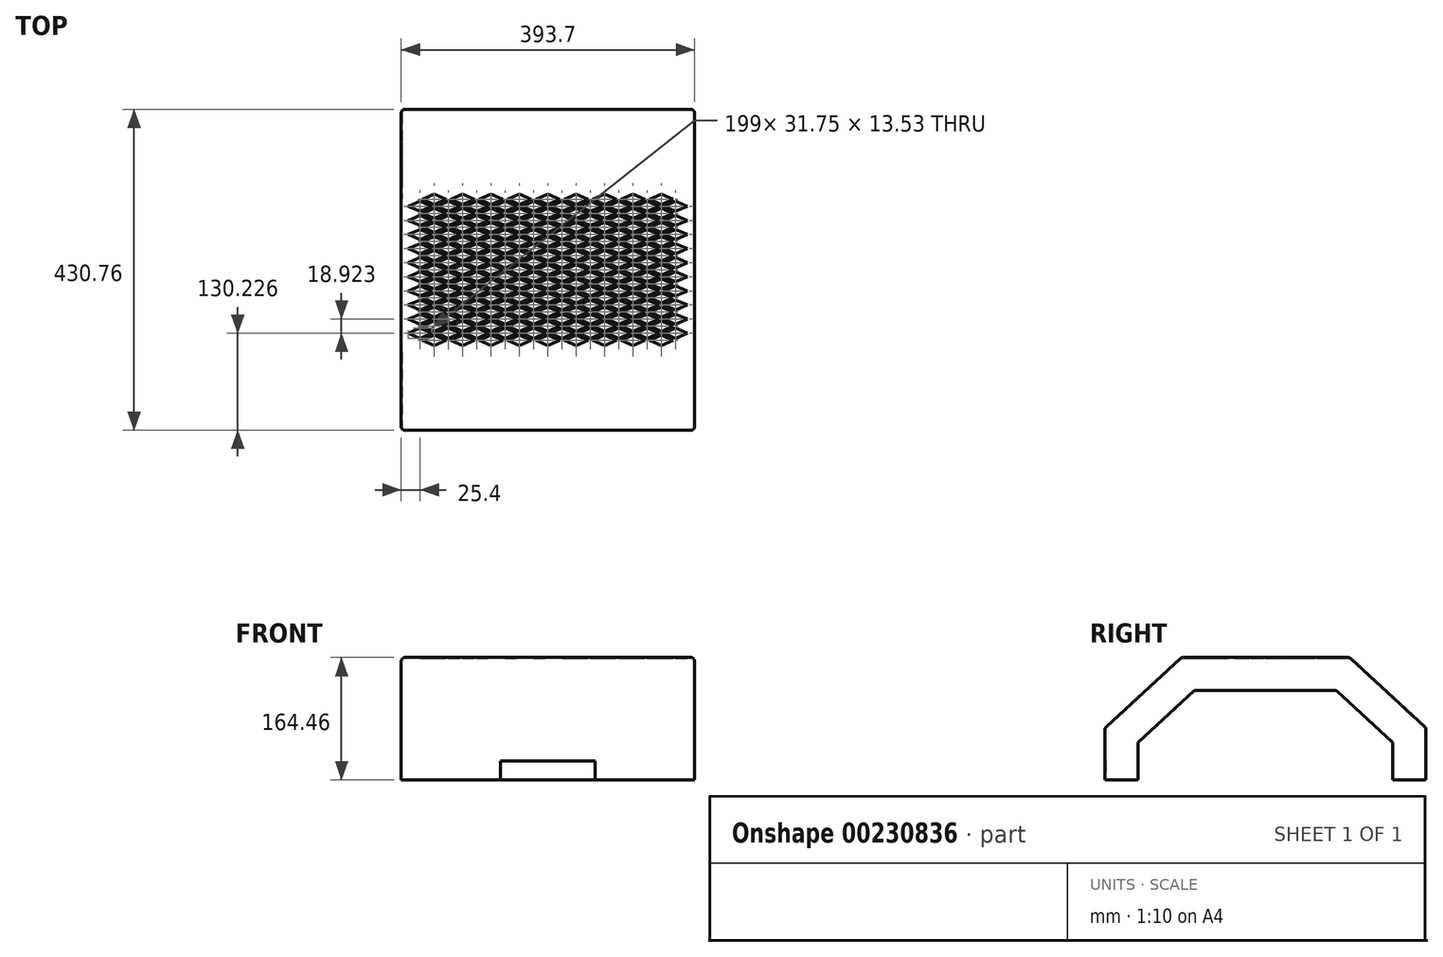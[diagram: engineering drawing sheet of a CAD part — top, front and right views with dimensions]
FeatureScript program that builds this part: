
annotation { "Feature Type Name" : "Feature", "Feature Type Description" : "" }
export const myFeature = defineFeature(function(context is Context, id is Id, definition is map)
    precondition{}
    {
        {
            var Q0;
            Q0=qCreatedBy(makeId("Right.planeOp"),FACE);
            var sketch = newSketch(context, id + "F0", { "sketchPlane" : qUnion([Q0])});
            skLineSegment(sketch, "E0", {"start": v(0, 0) * mm, "end": v(0, 169.27) * mm, "construction": true});
            skLineSegment(sketch, "E1", {"start": v(0, 164.46) * mm, "end": v(112.6, 164.46) * mm});
            skLineSegment(sketch, "E2", {"start": v(112.6, 164.46) * mm, "end": v(215.38, 69.85) * mm});
            skLineSegment(sketch, "E3", {"start": v(215.38, 69.85) * mm, "end": v(215.38, 0) * mm});
            skLineSegment(sketch, "E4", {"start": v(215.38, 0) * mm, "end": v(170.93, 0) * mm});
            skLineSegment(sketch, "E5", {"start": v(170.93, 0) * mm, "end": v(170.93, 50.35) * mm});
            skLineSegment(sketch, "E6", {"start": v(170.93, 50.35) * mm, "end": v(95.25, 120.01) * mm});
            skLineSegment(sketch, "E7", {"start": v(95.25, 120.01) * mm, "end": v(0, 120.01) * mm});
            skLineSegment(sketch, "E8.MirrorCS", {"start": v(0, 164.46) * mm, "end": v(-112.6, 164.46) * mm});
            skLineSegment(sketch, "E9.MirrorCS", {"start": v(-215.38, 0) * mm, "end": v(-170.93, 0) * mm});
            skLineSegment(sketch, "E10.MirrorCS", {"start": v(-170.93, 0) * mm, "end": v(-170.93, 50.35) * mm});
            skLineSegment(sketch, "E11.MirrorCS", {"start": v(-215.38, 69.85) * mm, "end": v(-215.38, 0) * mm});
            skLineSegment(sketch, "E12.MirrorCS", {"start": v(-95.25, 120.01) * mm, "end": v(0, 120.01) * mm});
            skLineSegment(sketch, "E13.MirrorCS", {"start": v(-112.6, 164.46) * mm, "end": v(-215.38, 69.85) * mm});
            skLineSegment(sketch, "E14.MirrorCS", {"start": v(-170.93, 50.35) * mm, "end": v(-95.25, 120.01) * mm});
            skSolve(sketch);
        }
        {
            var Q0;
            Q0=qSketchRegion(id+"F0",true);
            extrude(context, id + "F1", {"entities" : qUnion([Q0]), "endBound" : BoundingType.SYMMETRIC, "depth" : 393.7 * mm});
        }
        {
            var Q0;
            Q0=makeQuery(id+"F1.opExtrude","CAP_EDGE",EDGE,{"disambiguationData":[OSD([sQuery(id+"F0.wireOp",EDGE,"E1"),sQuery(id+"F0.wireOp",EDGE,"E8.MirrorCS")])],"isStart":true});
            var Q1;
            Q1=makeQuery(id+"F1.opExtrude","CAP_EDGE",EDGE,{"disambiguationData":[OSD([sQuery(id+"F0.wireOp",EDGE,"E1"),sQuery(id+"F0.wireOp",EDGE,"E8.MirrorCS")])],"isStart":false});
            var Q2;
            Q2=makeQuery(id+"F1.opExtrude","CAP_EDGE",EDGE,{"disambiguationData":[OSD([sQuery(id+"F0.wireOp",EDGE,"E13.MirrorCS")])],"isStart":false});
            var Q3;
            Q3=makeQuery(id+"F1.opExtrude","CAP_EDGE",EDGE,{"disambiguationData":[OSD([sQuery(id+"F0.wireOp",EDGE,"E11.MirrorCS")])],"isStart":false});
            var Q4;
            Q4=makeQuery(id+"F1.opExtrude","CAP_EDGE",EDGE,{"disambiguationData":[OSD([sQuery(id+"F0.wireOp",EDGE,"E2")])],"isStart":false});
            var Q5;
            Q5=makeQuery(id+"F1.opExtrude","CAP_EDGE",EDGE,{"disambiguationData":[OSD([sQuery(id+"F0.wireOp",EDGE,"E3")])],"isStart":false});
            var Q6;
            Q6=makeQuery(id+"F1.opExtrude","CAP_EDGE",EDGE,{"disambiguationData":[OSD([sQuery(id+"F0.wireOp",EDGE,"E3")])],"isStart":true});
            var Q7;
            Q7=makeQuery(id+"F1.opExtrude","CAP_EDGE",EDGE,{"disambiguationData":[OSD([sQuery(id+"F0.wireOp",EDGE,"E2")])],"isStart":true});
            var Q8;
            Q8=makeQuery(id+"F1.opExtrude","CAP_EDGE",EDGE,{"disambiguationData":[OSD([sQuery(id+"F0.wireOp",EDGE,"E13.MirrorCS")])],"isStart":true});
            var Q9;
            Q9=makeQuery(id+"F1.opExtrude","CAP_EDGE",EDGE,{"disambiguationData":[OSD([sQuery(id+"F0.wireOp",EDGE,"E11.MirrorCS")])],"isStart":true});
            var Q10;
            Q10=makeQuery(id+"F1.opExtrude","SWEPT_EDGE",EDGE,{"disambiguationData":[OSD([sQuery(id+"F0.wireOp",EDGE,"E11.MirrorCS"),sQuery(id+"F0.wireOp",EDGE,"E13.MirrorCS")])]});
            var Q11;
            Q11=makeQuery(id+"F1.opExtrude","SWEPT_EDGE",EDGE,{"disambiguationData":[OSD([sQuery(id+"F0.wireOp",EDGE,"E8.MirrorCS"),sQuery(id+"F0.wireOp",EDGE,"E13.MirrorCS")])]});
            var Q12;
            Q12=makeQuery(id+"F1.opExtrude","SWEPT_EDGE",EDGE,{"disambiguationData":[OSD([sQuery(id+"F0.wireOp",EDGE,"E1"),sQuery(id+"F0.wireOp",EDGE,"E2")])]});
            var Q13;
            Q13=makeQuery(id+"F1.opExtrude","SWEPT_EDGE",EDGE,{"disambiguationData":[OSD([sQuery(id+"F0.wireOp",EDGE,"E2"),sQuery(id+"F0.wireOp",EDGE,"E3")])]});
            fillet(context, id + "F2", {"entities" : qUnion([Q0, Q1, Q2, Q3, Q4, Q5, Q6, Q7, Q8, Q9, Q10, Q11, Q12, Q13]), "radius" : 5.08 * mm, "tangentPropagation" : true, "allowEdgeOverflow" : false});
        }
        {
            var Q0;
            Q0=makeQuery(id+"F1.opExtrude","SWEPT_FACE",FACE,{"disambiguationData":[OSD([sQuery(id+"F0.wireOp",EDGE,"E7"),sQuery(id+"F0.wireOp",EDGE,"E12.MirrorCS")])]});
            var Q1;
            Q1=makeQuery(id+"F1.opExtrude","SWEPT_FACE",FACE,{"disambiguationData":[OSD([sQuery(id+"F0.wireOp",EDGE,"E6")])]});
            var Q2;
            Q2=makeQuery(id+"F1.opExtrude","SWEPT_FACE",FACE,{"disambiguationData":[OSD([sQuery(id+"F0.wireOp",EDGE,"E5")])]});
            var Q3;
            Q3=makeQuery(id+"F1.opExtrude","SWEPT_FACE",FACE,{"disambiguationData":[OSD([sQuery(id+"F0.wireOp",EDGE,"E4")])]});
            var Q4;
            Q4=makeQuery(id+"F1.opExtrude","SWEPT_FACE",FACE,{"disambiguationData":[OSD([sQuery(id+"F0.wireOp",EDGE,"E14.MirrorCS")])]});
            var Q5;
            Q5=makeQuery(id+"F1.opExtrude","SWEPT_FACE",FACE,{"disambiguationData":[OSD([sQuery(id+"F0.wireOp",EDGE,"E10.MirrorCS")])]});
            var Q6;
            Q6=makeQuery(id+"F1.opExtrude","SWEPT_FACE",FACE,{"disambiguationData":[OSD([sQuery(id+"F0.wireOp",EDGE,"E9.MirrorCS")])]});
            shell(context, id + "F3", {"entities" : qUnion([Q0, Q1, Q2, Q3, Q4, Q5, Q6]), "thickness" : 0.95 * mm});
        }
        {
            var Q0;
            Q0=makeQuery(id+"F1.opExtrude","SWEPT_FACE",FACE,{"disambiguationData":[OSD([sQuery(id+"F0.wireOp",EDGE,"E11.MirrorCS")])]});
            var sketch = newSketch(context, id + "F4", { "sketchPlane" : qUnion([Q0])});
            skLineSegment(sketch, "E15.bottom", {"start": v(-63.5, 0) * mm, "end": v(63.5, 0) * mm});
            skLineSegment(sketch, "E15.top", {"start": v(-63.5, 25.4) * mm, "end": v(63.5, 25.4) * mm});
            skLineSegment(sketch, "E15.left", {"start": v(-63.5, 0) * mm, "end": v(-63.5, 25.4) * mm});
            skLineSegment(sketch, "E15.right", {"start": v(63.5, 0) * mm, "end": v(63.5, 25.4) * mm});
            skSolve(sketch);
        }
        {
            var Q0;
            Q0=qSketchRegion(id+"F4",true);
            extrude(context, id + "F5", {"entities" : qUnion([Q0]), "operationType" : NewBodyOperationType.REMOVE, "oppositeDirection" : true, "depth" : 25.4 * mm});
        }
        {
            var Q0;
            Q0=makeQuery(id+"F1.opExtrude","SWEPT_FACE",FACE,{"disambiguationData":[OSD([sQuery(id+"F0.wireOp",EDGE,"E1"),sQuery(id+"F0.wireOp",EDGE,"E8.MirrorCS")])]});
            var sketch = newSketch(context, id + "F6", { "sketchPlane" : qUnion([Q0])});
            skLineSegment(sketch, "E16", {"start": v(-15.88, 0) * mm, "end": v(0, 6.76) * mm});
            skLineSegment(sketch, "E17", {"start": v(0, 6.76) * mm, "end": v(15.88, 0) * mm});
            skLineSegment(sketch, "E18", {"start": v(15.88, 0) * mm, "end": v(0, -6.76) * mm});
            skLineSegment(sketch, "E19", {"start": v(0, -6.76) * mm, "end": v(-15.88, 0) * mm});
            skLineSegment(sketch, "E20.0.1.0", {"start": v(-15.88, 18.92) * mm, "end": v(0, 25.69) * mm});
            skLineSegment(sketch, "E20.0.1.1", {"start": v(15.88, 18.92) * mm, "end": v(0, 12.16) * mm});
            skLineSegment(sketch, "E20.0.1.2", {"start": v(0, 12.16) * mm, "end": v(-15.88, 18.92) * mm});
            skLineSegment(sketch, "E20.0.1.3", {"start": v(0, 25.69) * mm, "end": v(15.88, 18.92) * mm});
            skLineSegment(sketch, "E20.0.2.0", {"start": v(-15.88, 37.85) * mm, "end": v(0, 44.6) * mm});
            skLineSegment(sketch, "E20.0.2.1", {"start": v(15.88, 37.85) * mm, "end": v(0, 31.08) * mm});
            skLineSegment(sketch, "E20.0.2.2", {"start": v(0, 31.08) * mm, "end": v(-15.88, 37.85) * mm});
            skLineSegment(sketch, "E20.0.2.3", {"start": v(0, 44.6) * mm, "end": v(15.88, 37.85) * mm});
            skLineSegment(sketch, "E20.0.3.0", {"start": v(-15.88, 56.77) * mm, "end": v(0, 63.53) * mm});
            skLineSegment(sketch, "E20.0.3.1", {"start": v(15.88, 56.77) * mm, "end": v(0, 50) * mm});
            skLineSegment(sketch, "E20.0.3.2", {"start": v(0, 50) * mm, "end": v(-15.88, 56.77) * mm});
            skLineSegment(sketch, "E20.0.3.3", {"start": v(0, 63.53) * mm, "end": v(15.88, 56.77) * mm});
            skLineSegment(sketch, "E20.0.4.0", {"start": v(-15.88, 75.7) * mm, "end": v(0, 82.45) * mm});
            skLineSegment(sketch, "E20.0.4.1", {"start": v(15.88, 75.7) * mm, "end": v(0, 68.93) * mm});
            skLineSegment(sketch, "E20.0.4.2", {"start": v(0, 68.93) * mm, "end": v(-15.88, 75.7) * mm});
            skLineSegment(sketch, "E20.0.4.3", {"start": v(0, 82.45) * mm, "end": v(15.88, 75.7) * mm});
            skLineSegment(sketch, "E20.0.5.0", {"start": v(-15.88, 94.62) * mm, "end": v(0, 101.38) * mm});
            skLineSegment(sketch, "E20.0.5.1", {"start": v(15.88, 94.62) * mm, "end": v(0, 87.85) * mm});
            skLineSegment(sketch, "E20.0.5.2", {"start": v(0, 87.85) * mm, "end": v(-15.88, 94.62) * mm});
            skLineSegment(sketch, "E20.0.5.3", {"start": v(0, 101.38) * mm, "end": v(15.88, 94.62) * mm});
            skLineSegment(sketch, "E20.1.0.0", {"start": v(22.23, 0) * mm, "end": v(38.1, 6.76) * mm});
            skLineSegment(sketch, "E20.1.0.1", {"start": v(53.98, 0) * mm, "end": v(38.1, -6.76) * mm});
            skLineSegment(sketch, "E20.1.0.2", {"start": v(38.1, -6.76) * mm, "end": v(22.22, 0) * mm});
            skLineSegment(sketch, "E20.1.0.3", {"start": v(38.1, 6.76) * mm, "end": v(53.98, 0) * mm});
            skLineSegment(sketch, "E20.1.1.0", {"start": v(22.23, 18.92) * mm, "end": v(38.1, 25.69) * mm});
            skLineSegment(sketch, "E20.1.1.1", {"start": v(53.98, 18.92) * mm, "end": v(38.1, 12.16) * mm});
            skLineSegment(sketch, "E20.1.1.2", {"start": v(38.1, 12.16) * mm, "end": v(22.22, 18.92) * mm});
            skLineSegment(sketch, "E20.1.1.3", {"start": v(38.1, 25.69) * mm, "end": v(53.98, 18.92) * mm});
            skLineSegment(sketch, "E20.1.2.0", {"start": v(22.23, 37.85) * mm, "end": v(38.1, 44.6) * mm});
            skLineSegment(sketch, "E20.1.2.1", {"start": v(53.98, 37.85) * mm, "end": v(38.1, 31.08) * mm});
            skLineSegment(sketch, "E20.1.2.2", {"start": v(38.1, 31.08) * mm, "end": v(22.22, 37.85) * mm});
            skLineSegment(sketch, "E20.1.2.3", {"start": v(38.1, 44.6) * mm, "end": v(53.98, 37.85) * mm});
            skLineSegment(sketch, "E20.1.3.0", {"start": v(22.23, 56.77) * mm, "end": v(38.1, 63.53) * mm});
            skLineSegment(sketch, "E20.1.3.1", {"start": v(53.98, 56.77) * mm, "end": v(38.1, 50) * mm});
            skLineSegment(sketch, "E20.1.3.2", {"start": v(38.1, 50) * mm, "end": v(22.22, 56.77) * mm});
            skLineSegment(sketch, "E20.1.3.3", {"start": v(38.1, 63.53) * mm, "end": v(53.98, 56.77) * mm});
            skLineSegment(sketch, "E20.1.4.0", {"start": v(22.23, 75.7) * mm, "end": v(38.1, 82.45) * mm});
            skLineSegment(sketch, "E20.1.4.1", {"start": v(53.98, 75.7) * mm, "end": v(38.1, 68.93) * mm});
            skLineSegment(sketch, "E20.1.4.2", {"start": v(38.1, 68.93) * mm, "end": v(22.22, 75.7) * mm});
            skLineSegment(sketch, "E20.1.4.3", {"start": v(38.1, 82.45) * mm, "end": v(53.98, 75.7) * mm});
            skLineSegment(sketch, "E20.1.5.0", {"start": v(22.23, 94.62) * mm, "end": v(38.1, 101.38) * mm});
            skLineSegment(sketch, "E20.1.5.1", {"start": v(53.98, 94.62) * mm, "end": v(38.1, 87.85) * mm});
            skLineSegment(sketch, "E20.1.5.2", {"start": v(38.1, 87.85) * mm, "end": v(22.22, 94.62) * mm});
            skLineSegment(sketch, "E20.1.5.3", {"start": v(38.1, 101.38) * mm, "end": v(53.98, 94.62) * mm});
            skLineSegment(sketch, "E20.2.0.0", {"start": v(60.33, 0) * mm, "end": v(76.2, 6.76) * mm});
            skLineSegment(sketch, "E20.2.0.1", {"start": v(92.08, 0) * mm, "end": v(76.2, -6.76) * mm});
            skLineSegment(sketch, "E20.2.0.2", {"start": v(76.2, -6.76) * mm, "end": v(60.33, 0) * mm});
            skLineSegment(sketch, "E20.2.0.3", {"start": v(76.2, 6.76) * mm, "end": v(92.08, 0) * mm});
            skLineSegment(sketch, "E20.2.1.0", {"start": v(60.33, 18.92) * mm, "end": v(76.2, 25.69) * mm});
            skLineSegment(sketch, "E20.2.1.1", {"start": v(92.08, 18.92) * mm, "end": v(76.2, 12.16) * mm});
            skLineSegment(sketch, "E20.2.1.2", {"start": v(76.2, 12.16) * mm, "end": v(60.33, 18.92) * mm});
            skLineSegment(sketch, "E20.2.1.3", {"start": v(76.2, 25.69) * mm, "end": v(92.08, 18.92) * mm});
            skLineSegment(sketch, "E20.2.2.0", {"start": v(60.33, 37.85) * mm, "end": v(76.2, 44.6) * mm});
            skLineSegment(sketch, "E20.2.2.1", {"start": v(92.08, 37.85) * mm, "end": v(76.2, 31.08) * mm});
            skLineSegment(sketch, "E20.2.2.2", {"start": v(76.2, 31.08) * mm, "end": v(60.33, 37.85) * mm});
            skLineSegment(sketch, "E20.2.2.3", {"start": v(76.2, 44.6) * mm, "end": v(92.08, 37.85) * mm});
            skLineSegment(sketch, "E20.2.3.0", {"start": v(60.33, 56.77) * mm, "end": v(76.2, 63.53) * mm});
            skLineSegment(sketch, "E20.2.3.1", {"start": v(92.08, 56.77) * mm, "end": v(76.2, 50) * mm});
            skLineSegment(sketch, "E20.2.3.2", {"start": v(76.2, 50) * mm, "end": v(60.33, 56.77) * mm});
            skLineSegment(sketch, "E20.2.3.3", {"start": v(76.2, 63.53) * mm, "end": v(92.08, 56.77) * mm});
            skLineSegment(sketch, "E20.2.4.0", {"start": v(60.33, 75.7) * mm, "end": v(76.2, 82.45) * mm});
            skLineSegment(sketch, "E20.2.4.1", {"start": v(92.08, 75.7) * mm, "end": v(76.2, 68.93) * mm});
            skLineSegment(sketch, "E20.2.4.2", {"start": v(76.2, 68.93) * mm, "end": v(60.33, 75.7) * mm});
            skLineSegment(sketch, "E20.2.4.3", {"start": v(76.2, 82.45) * mm, "end": v(92.08, 75.7) * mm});
            skLineSegment(sketch, "E20.2.5.0", {"start": v(60.33, 94.62) * mm, "end": v(76.2, 101.38) * mm});
            skLineSegment(sketch, "E20.2.5.1", {"start": v(92.08, 94.62) * mm, "end": v(76.2, 87.85) * mm});
            skLineSegment(sketch, "E20.2.5.2", {"start": v(76.2, 87.85) * mm, "end": v(60.33, 94.62) * mm});
            skLineSegment(sketch, "E20.2.5.3", {"start": v(76.2, 101.38) * mm, "end": v(92.08, 94.62) * mm});
            skLineSegment(sketch, "E20.3.0.0", {"start": v(98.43, 0) * mm, "end": v(114.3, 6.76) * mm});
            skLineSegment(sketch, "E20.3.0.1", {"start": v(130.18, 0) * mm, "end": v(114.3, -6.76) * mm});
            skLineSegment(sketch, "E20.3.0.2", {"start": v(114.3, -6.76) * mm, "end": v(98.43, 0) * mm});
            skLineSegment(sketch, "E20.3.0.3", {"start": v(114.3, 6.76) * mm, "end": v(130.18, 0) * mm});
            skLineSegment(sketch, "E20.3.1.0", {"start": v(98.43, 18.92) * mm, "end": v(114.3, 25.69) * mm});
            skLineSegment(sketch, "E20.3.1.1", {"start": v(130.18, 18.92) * mm, "end": v(114.3, 12.16) * mm});
            skLineSegment(sketch, "E20.3.1.2", {"start": v(114.3, 12.16) * mm, "end": v(98.43, 18.92) * mm});
            skLineSegment(sketch, "E20.3.1.3", {"start": v(114.3, 25.69) * mm, "end": v(130.18, 18.92) * mm});
            skLineSegment(sketch, "E20.3.2.0", {"start": v(98.43, 37.85) * mm, "end": v(114.3, 44.6) * mm});
            skLineSegment(sketch, "E20.3.2.1", {"start": v(130.18, 37.85) * mm, "end": v(114.3, 31.08) * mm});
            skLineSegment(sketch, "E20.3.2.2", {"start": v(114.3, 31.08) * mm, "end": v(98.43, 37.85) * mm});
            skLineSegment(sketch, "E20.3.2.3", {"start": v(114.3, 44.6) * mm, "end": v(130.18, 37.85) * mm});
            skLineSegment(sketch, "E20.3.3.0", {"start": v(98.43, 56.77) * mm, "end": v(114.3, 63.53) * mm});
            skLineSegment(sketch, "E20.3.3.1", {"start": v(130.18, 56.77) * mm, "end": v(114.3, 50) * mm});
            skLineSegment(sketch, "E20.3.3.2", {"start": v(114.3, 50) * mm, "end": v(98.43, 56.77) * mm});
            skLineSegment(sketch, "E20.3.3.3", {"start": v(114.3, 63.53) * mm, "end": v(130.18, 56.77) * mm});
            skLineSegment(sketch, "E20.3.4.0", {"start": v(98.43, 75.7) * mm, "end": v(114.3, 82.45) * mm});
            skLineSegment(sketch, "E20.3.4.1", {"start": v(130.18, 75.7) * mm, "end": v(114.3, 68.93) * mm});
            skLineSegment(sketch, "E20.3.4.2", {"start": v(114.3, 68.93) * mm, "end": v(98.43, 75.7) * mm});
            skLineSegment(sketch, "E20.3.4.3", {"start": v(114.3, 82.45) * mm, "end": v(130.18, 75.7) * mm});
            skLineSegment(sketch, "E20.3.5.0", {"start": v(98.43, 94.62) * mm, "end": v(114.3, 101.38) * mm});
            skLineSegment(sketch, "E20.3.5.1", {"start": v(130.18, 94.62) * mm, "end": v(114.3, 87.85) * mm});
            skLineSegment(sketch, "E20.3.5.2", {"start": v(114.3, 87.85) * mm, "end": v(98.43, 94.62) * mm});
            skLineSegment(sketch, "E20.3.5.3", {"start": v(114.3, 101.38) * mm, "end": v(130.18, 94.62) * mm});
            skLineSegment(sketch, "E20.4.0.0", {"start": v(136.53, 0) * mm, "end": v(152.4, 6.76) * mm});
            skLineSegment(sketch, "E20.4.0.1", {"start": v(168.28, 0) * mm, "end": v(152.4, -6.76) * mm});
            skLineSegment(sketch, "E20.4.0.2", {"start": v(152.4, -6.76) * mm, "end": v(136.53, 0) * mm});
            skLineSegment(sketch, "E20.4.0.3", {"start": v(152.4, 6.76) * mm, "end": v(168.28, 0) * mm});
            skLineSegment(sketch, "E20.4.1.0", {"start": v(136.53, 18.92) * mm, "end": v(152.4, 25.69) * mm});
            skLineSegment(sketch, "E20.4.1.1", {"start": v(168.28, 18.92) * mm, "end": v(152.4, 12.16) * mm});
            skLineSegment(sketch, "E20.4.1.2", {"start": v(152.4, 12.16) * mm, "end": v(136.53, 18.92) * mm});
            skLineSegment(sketch, "E20.4.1.3", {"start": v(152.4, 25.69) * mm, "end": v(168.28, 18.92) * mm});
            skLineSegment(sketch, "E20.4.2.0", {"start": v(136.53, 37.85) * mm, "end": v(152.4, 44.6) * mm});
            skLineSegment(sketch, "E20.4.2.1", {"start": v(168.28, 37.85) * mm, "end": v(152.4, 31.08) * mm});
            skLineSegment(sketch, "E20.4.2.2", {"start": v(152.4, 31.08) * mm, "end": v(136.53, 37.85) * mm});
            skLineSegment(sketch, "E20.4.2.3", {"start": v(152.4, 44.6) * mm, "end": v(168.28, 37.85) * mm});
            skLineSegment(sketch, "E20.4.3.0", {"start": v(136.53, 56.77) * mm, "end": v(152.4, 63.53) * mm});
            skLineSegment(sketch, "E20.4.3.1", {"start": v(168.28, 56.77) * mm, "end": v(152.4, 50) * mm});
            skLineSegment(sketch, "E20.4.3.2", {"start": v(152.4, 50) * mm, "end": v(136.53, 56.77) * mm});
            skLineSegment(sketch, "E20.4.3.3", {"start": v(152.4, 63.53) * mm, "end": v(168.28, 56.77) * mm});
            skLineSegment(sketch, "E20.4.4.0", {"start": v(136.53, 75.7) * mm, "end": v(152.4, 82.45) * mm});
            skLineSegment(sketch, "E20.4.4.1", {"start": v(168.28, 75.7) * mm, "end": v(152.4, 68.93) * mm});
            skLineSegment(sketch, "E20.4.4.2", {"start": v(152.4, 68.93) * mm, "end": v(136.53, 75.7) * mm});
            skLineSegment(sketch, "E20.4.4.3", {"start": v(152.4, 82.45) * mm, "end": v(168.28, 75.7) * mm});
            skLineSegment(sketch, "E20.4.5.0", {"start": v(136.53, 94.62) * mm, "end": v(152.4, 101.38) * mm});
            skLineSegment(sketch, "E20.4.5.1", {"start": v(168.28, 94.62) * mm, "end": v(152.4, 87.85) * mm});
            skLineSegment(sketch, "E20.4.5.2", {"start": v(152.4, 87.85) * mm, "end": v(136.53, 94.62) * mm});
            skLineSegment(sketch, "E20.4.5.3", {"start": v(152.4, 101.38) * mm, "end": v(168.28, 94.62) * mm});
            skLineSegment(sketch, "E20.direction1", {"start": v(-15.88, 0) * mm, "end": v(22.22, 0) * mm, "construction": true});
            skLineSegment(sketch, "E20.direction2", {"start": v(-15.88, 0) * mm, "end": v(-15.88, 18.92) * mm, "construction": true});
            skLineSegment(sketch, "E21.0.1.0", {"start": v(0, -25.69) * mm, "end": v(-15.88, -18.92) * mm});
            skLineSegment(sketch, "E21.0.1.1", {"start": v(15.88, -18.92) * mm, "end": v(0, -25.69) * mm});
            skLineSegment(sketch, "E21.0.1.2", {"start": v(0, -12.16) * mm, "end": v(15.88, -18.92) * mm});
            skLineSegment(sketch, "E21.0.1.3", {"start": v(-15.88, -18.92) * mm, "end": v(0, -12.16) * mm});
            skLineSegment(sketch, "E21.0.1.4", {"start": v(114.3, -12.16) * mm, "end": v(130.18, -18.92) * mm});
            skLineSegment(sketch, "E21.0.1.5", {"start": v(38.1, -12.16) * mm, "end": v(53.98, -18.92) * mm});
            skLineSegment(sketch, "E21.0.1.6", {"start": v(152.4, -12.16) * mm, "end": v(168.28, -18.92) * mm});
            skLineSegment(sketch, "E21.0.1.7", {"start": v(76.2, -12.16) * mm, "end": v(92.08, -18.92) * mm});
            skLineSegment(sketch, "E21.0.1.8", {"start": v(114.3, -25.69) * mm, "end": v(98.43, -18.92) * mm});
            skLineSegment(sketch, "E21.0.1.9", {"start": v(38.1, -25.69) * mm, "end": v(22.22, -18.92) * mm});
            skLineSegment(sketch, "E21.0.1.10", {"start": v(76.2, -25.69) * mm, "end": v(60.33, -18.92) * mm});
            skLineSegment(sketch, "E21.0.1.11", {"start": v(130.18, -18.92) * mm, "end": v(114.3, -25.69) * mm});
            skLineSegment(sketch, "E21.0.1.12", {"start": v(53.98, -18.92) * mm, "end": v(38.1, -25.69) * mm});
            skLineSegment(sketch, "E21.0.1.13", {"start": v(152.4, -25.69) * mm, "end": v(136.53, -18.92) * mm});
            skLineSegment(sketch, "E21.0.1.14", {"start": v(98.43, -18.92) * mm, "end": v(114.3, -12.16) * mm});
            skLineSegment(sketch, "E21.0.1.15", {"start": v(-15.88, -18.92) * mm, "end": v(22.22, -18.92) * mm, "construction": true});
            skLineSegment(sketch, "E21.0.1.16", {"start": v(22.23, -18.92) * mm, "end": v(38.1, -12.16) * mm});
            skLineSegment(sketch, "E21.0.1.17", {"start": v(168.28, -18.92) * mm, "end": v(152.4, -25.69) * mm});
            skLineSegment(sketch, "E21.0.1.18", {"start": v(92.08, -18.92) * mm, "end": v(76.2, -25.69) * mm});
            skLineSegment(sketch, "E21.0.1.19", {"start": v(136.53, -18.92) * mm, "end": v(152.4, -12.16) * mm});
            skLineSegment(sketch, "E21.0.1.20", {"start": v(60.33, -18.92) * mm, "end": v(76.2, -12.16) * mm});
            skLineSegment(sketch, "E21.0.2.0", {"start": v(0, -44.6) * mm, "end": v(-15.88, -37.85) * mm});
            skLineSegment(sketch, "E21.0.2.1", {"start": v(15.88, -37.85) * mm, "end": v(0, -44.6) * mm});
            skLineSegment(sketch, "E21.0.2.2", {"start": v(0, -31.08) * mm, "end": v(15.88, -37.85) * mm});
            skLineSegment(sketch, "E21.0.2.3", {"start": v(-15.88, -37.85) * mm, "end": v(0, -31.08) * mm});
            skLineSegment(sketch, "E21.0.2.4", {"start": v(114.3, -31.08) * mm, "end": v(130.18, -37.85) * mm});
            skLineSegment(sketch, "E21.0.2.5", {"start": v(38.1, -31.08) * mm, "end": v(53.98, -37.85) * mm});
            skLineSegment(sketch, "E21.0.2.6", {"start": v(152.4, -31.08) * mm, "end": v(168.28, -37.85) * mm});
            skLineSegment(sketch, "E21.0.2.7", {"start": v(76.2, -31.08) * mm, "end": v(92.08, -37.85) * mm});
            skLineSegment(sketch, "E21.0.2.8", {"start": v(114.3, -44.6) * mm, "end": v(98.43, -37.85) * mm});
            skLineSegment(sketch, "E21.0.2.9", {"start": v(38.1, -44.6) * mm, "end": v(22.22, -37.85) * mm});
            skLineSegment(sketch, "E21.0.2.10", {"start": v(76.2, -44.6) * mm, "end": v(60.33, -37.85) * mm});
            skLineSegment(sketch, "E21.0.2.11", {"start": v(130.18, -37.85) * mm, "end": v(114.3, -44.6) * mm});
            skLineSegment(sketch, "E21.0.2.12", {"start": v(53.98, -37.85) * mm, "end": v(38.1, -44.6) * mm});
            skLineSegment(sketch, "E21.0.2.13", {"start": v(152.4, -44.6) * mm, "end": v(136.53, -37.85) * mm});
            skLineSegment(sketch, "E21.0.2.14", {"start": v(98.43, -37.85) * mm, "end": v(114.3, -31.08) * mm});
            skLineSegment(sketch, "E21.0.2.15", {"start": v(-15.88, -37.85) * mm, "end": v(22.22, -37.85) * mm, "construction": true});
            skLineSegment(sketch, "E21.0.2.16", {"start": v(22.23, -37.85) * mm, "end": v(38.1, -31.08) * mm});
            skLineSegment(sketch, "E21.0.2.17", {"start": v(168.28, -37.85) * mm, "end": v(152.4, -44.6) * mm});
            skLineSegment(sketch, "E21.0.2.18", {"start": v(92.08, -37.85) * mm, "end": v(76.2, -44.6) * mm});
            skLineSegment(sketch, "E21.0.2.19", {"start": v(136.53, -37.85) * mm, "end": v(152.4, -31.08) * mm});
            skLineSegment(sketch, "E21.0.2.20", {"start": v(60.33, -37.85) * mm, "end": v(76.2, -31.08) * mm});
            skLineSegment(sketch, "E21.0.3.0", {"start": v(0, -63.53) * mm, "end": v(-15.88, -56.77) * mm});
            skLineSegment(sketch, "E21.0.3.1", {"start": v(15.88, -56.77) * mm, "end": v(0, -63.53) * mm});
            skLineSegment(sketch, "E21.0.3.2", {"start": v(0, -50) * mm, "end": v(15.88, -56.77) * mm});
            skLineSegment(sketch, "E21.0.3.3", {"start": v(-15.88, -56.77) * mm, "end": v(0, -50) * mm});
            skLineSegment(sketch, "E21.0.3.4", {"start": v(114.3, -50) * mm, "end": v(130.18, -56.77) * mm});
            skLineSegment(sketch, "E21.0.3.5", {"start": v(38.1, -50) * mm, "end": v(53.98, -56.77) * mm});
            skLineSegment(sketch, "E21.0.3.6", {"start": v(152.4, -50) * mm, "end": v(168.28, -56.77) * mm});
            skLineSegment(sketch, "E21.0.3.7", {"start": v(76.2, -50) * mm, "end": v(92.08, -56.77) * mm});
            skLineSegment(sketch, "E21.0.3.8", {"start": v(114.3, -63.53) * mm, "end": v(98.43, -56.77) * mm});
            skLineSegment(sketch, "E21.0.3.9", {"start": v(38.1, -63.53) * mm, "end": v(22.22, -56.77) * mm});
            skLineSegment(sketch, "E21.0.3.10", {"start": v(76.2, -63.53) * mm, "end": v(60.33, -56.77) * mm});
            skLineSegment(sketch, "E21.0.3.11", {"start": v(130.18, -56.77) * mm, "end": v(114.3, -63.53) * mm});
            skLineSegment(sketch, "E21.0.3.12", {"start": v(53.98, -56.77) * mm, "end": v(38.1, -63.53) * mm});
            skLineSegment(sketch, "E21.0.3.13", {"start": v(152.4, -63.53) * mm, "end": v(136.53, -56.77) * mm});
            skLineSegment(sketch, "E21.0.3.14", {"start": v(98.43, -56.77) * mm, "end": v(114.3, -50) * mm});
            skLineSegment(sketch, "E21.0.3.15", {"start": v(-15.88, -56.77) * mm, "end": v(22.22, -56.77) * mm, "construction": true});
            skLineSegment(sketch, "E21.0.3.16", {"start": v(22.23, -56.77) * mm, "end": v(38.1, -50) * mm});
            skLineSegment(sketch, "E21.0.3.17", {"start": v(168.28, -56.77) * mm, "end": v(152.4, -63.53) * mm});
            skLineSegment(sketch, "E21.0.3.18", {"start": v(92.08, -56.77) * mm, "end": v(76.2, -63.53) * mm});
            skLineSegment(sketch, "E21.0.3.19", {"start": v(136.53, -56.77) * mm, "end": v(152.4, -50) * mm});
            skLineSegment(sketch, "E21.0.3.20", {"start": v(60.33, -56.77) * mm, "end": v(76.2, -50) * mm});
            skLineSegment(sketch, "E21.0.4.0", {"start": v(0, -82.45) * mm, "end": v(-15.88, -75.7) * mm});
            skLineSegment(sketch, "E21.0.4.1", {"start": v(15.88, -75.7) * mm, "end": v(0, -82.45) * mm});
            skLineSegment(sketch, "E21.0.4.2", {"start": v(0, -68.93) * mm, "end": v(15.88, -75.7) * mm});
            skLineSegment(sketch, "E21.0.4.3", {"start": v(-15.88, -75.7) * mm, "end": v(0, -68.93) * mm});
            skLineSegment(sketch, "E21.0.4.4", {"start": v(114.3, -68.93) * mm, "end": v(130.18, -75.7) * mm});
            skLineSegment(sketch, "E21.0.4.5", {"start": v(38.1, -68.93) * mm, "end": v(53.98, -75.7) * mm});
            skLineSegment(sketch, "E21.0.4.6", {"start": v(152.4, -68.93) * mm, "end": v(168.28, -75.7) * mm});
            skLineSegment(sketch, "E21.0.4.7", {"start": v(76.2, -68.93) * mm, "end": v(92.08, -75.7) * mm});
            skLineSegment(sketch, "E21.0.4.8", {"start": v(114.3, -82.45) * mm, "end": v(98.43, -75.7) * mm});
            skLineSegment(sketch, "E21.0.4.9", {"start": v(38.1, -82.45) * mm, "end": v(22.22, -75.7) * mm});
            skLineSegment(sketch, "E21.0.4.10", {"start": v(76.2, -82.45) * mm, "end": v(60.33, -75.7) * mm});
            skLineSegment(sketch, "E21.0.4.11", {"start": v(130.18, -75.7) * mm, "end": v(114.3, -82.45) * mm});
            skLineSegment(sketch, "E21.0.4.12", {"start": v(53.98, -75.7) * mm, "end": v(38.1, -82.45) * mm});
            skLineSegment(sketch, "E21.0.4.13", {"start": v(152.4, -82.45) * mm, "end": v(136.53, -75.7) * mm});
            skLineSegment(sketch, "E21.0.4.14", {"start": v(98.43, -75.7) * mm, "end": v(114.3, -68.93) * mm});
            skLineSegment(sketch, "E21.0.4.15", {"start": v(-15.88, -75.7) * mm, "end": v(22.22, -75.7) * mm, "construction": true});
            skLineSegment(sketch, "E21.0.4.16", {"start": v(22.23, -75.7) * mm, "end": v(38.1, -68.93) * mm});
            skLineSegment(sketch, "E21.0.4.17", {"start": v(168.28, -75.7) * mm, "end": v(152.4, -82.45) * mm});
            skLineSegment(sketch, "E21.0.4.18", {"start": v(92.08, -75.7) * mm, "end": v(76.2, -82.45) * mm});
            skLineSegment(sketch, "E21.0.4.19", {"start": v(136.53, -75.7) * mm, "end": v(152.4, -68.93) * mm});
            skLineSegment(sketch, "E21.0.4.20", {"start": v(60.33, -75.7) * mm, "end": v(76.2, -68.93) * mm});
            skLineSegment(sketch, "E21.0.5.0", {"start": v(0, -101.38) * mm, "end": v(-15.88, -94.61) * mm});
            skLineSegment(sketch, "E21.0.5.1", {"start": v(15.88, -94.62) * mm, "end": v(0, -101.38) * mm});
            skLineSegment(sketch, "E21.0.5.2", {"start": v(0, -87.85) * mm, "end": v(15.88, -94.62) * mm});
            skLineSegment(sketch, "E21.0.5.3", {"start": v(-15.88, -94.62) * mm, "end": v(0, -87.85) * mm});
            skLineSegment(sketch, "E21.0.5.4", {"start": v(114.3, -87.85) * mm, "end": v(130.18, -94.62) * mm});
            skLineSegment(sketch, "E21.0.5.5", {"start": v(38.1, -87.85) * mm, "end": v(53.98, -94.62) * mm});
            skLineSegment(sketch, "E21.0.5.6", {"start": v(152.4, -87.85) * mm, "end": v(168.28, -94.62) * mm});
            skLineSegment(sketch, "E21.0.5.7", {"start": v(76.2, -87.85) * mm, "end": v(92.08, -94.62) * mm});
            skLineSegment(sketch, "E21.0.5.8", {"start": v(114.3, -101.38) * mm, "end": v(98.43, -94.61) * mm});
            skLineSegment(sketch, "E21.0.5.9", {"start": v(38.1, -101.38) * mm, "end": v(22.22, -94.61) * mm});
            skLineSegment(sketch, "E21.0.5.10", {"start": v(76.2, -101.38) * mm, "end": v(60.33, -94.61) * mm});
            skLineSegment(sketch, "E21.0.5.11", {"start": v(130.18, -94.62) * mm, "end": v(114.3, -101.38) * mm});
            skLineSegment(sketch, "E21.0.5.12", {"start": v(53.98, -94.62) * mm, "end": v(38.1, -101.38) * mm});
            skLineSegment(sketch, "E21.0.5.13", {"start": v(152.4, -101.38) * mm, "end": v(136.53, -94.61) * mm});
            skLineSegment(sketch, "E21.0.5.14", {"start": v(98.43, -94.62) * mm, "end": v(114.3, -87.85) * mm});
            skLineSegment(sketch, "E21.0.5.15", {"start": v(-15.88, -94.62) * mm, "end": v(22.22, -94.62) * mm, "construction": true});
            skLineSegment(sketch, "E21.0.5.16", {"start": v(22.23, -94.62) * mm, "end": v(38.1, -87.85) * mm});
            skLineSegment(sketch, "E21.0.5.17", {"start": v(168.28, -94.62) * mm, "end": v(152.4, -101.38) * mm});
            skLineSegment(sketch, "E21.0.5.18", {"start": v(92.08, -94.62) * mm, "end": v(76.2, -101.38) * mm});
            skLineSegment(sketch, "E21.0.5.19", {"start": v(136.53, -94.62) * mm, "end": v(152.4, -87.85) * mm});
            skLineSegment(sketch, "E21.0.5.20", {"start": v(60.33, -94.62) * mm, "end": v(76.2, -87.85) * mm});
            skLineSegment(sketch, "E21.direction1", {"start": v(-15.88, 0) * mm, "end": v(9.52, 0) * mm, "construction": true});
            skLineSegment(sketch, "E21.direction2", {"start": v(-15.88, 0) * mm, "end": v(-15.88, -18.92) * mm, "construction": true});
            skLineSegment(sketch, "E22.1.0.0", {"start": v(-38.1, -50) * mm, "end": v(-22.23, -56.77) * mm});
            skLineSegment(sketch, "E22.1.0.1", {"start": v(-38.1, 87.85) * mm, "end": v(-53.98, 94.62) * mm});
            skLineSegment(sketch, "E22.1.0.2", {"start": v(-53.98, 56.77) * mm, "end": v(-38.1, 63.53) * mm});
            skLineSegment(sketch, "E22.1.0.3", {"start": v(-38.1, 44.6) * mm, "end": v(-22.23, 37.85) * mm});
            skLineSegment(sketch, "E22.1.0.4", {"start": v(-38.1, 31.08) * mm, "end": v(-53.98, 37.85) * mm});
            skLineSegment(sketch, "E22.1.0.5", {"start": v(-22.23, 37.85) * mm, "end": v(-38.1, 31.08) * mm});
            skLineSegment(sketch, "E22.1.0.6", {"start": v(-53.98, 37.85) * mm, "end": v(-38.1, 44.6) * mm});
            skLineSegment(sketch, "E22.1.0.7", {"start": v(-38.1, 25.69) * mm, "end": v(-22.23, 18.92) * mm});
            skLineSegment(sketch, "E22.1.0.8", {"start": v(-38.1, 12.16) * mm, "end": v(-53.98, 18.92) * mm});
            skLineSegment(sketch, "E22.1.0.9", {"start": v(-22.23, 18.92) * mm, "end": v(-38.1, 12.16) * mm});
            skLineSegment(sketch, "E22.1.0.10", {"start": v(-53.98, 18.92) * mm, "end": v(-38.1, 25.69) * mm});
            skLineSegment(sketch, "E22.1.0.11", {"start": v(-38.1, -6.76) * mm, "end": v(-53.98, 0) * mm});
            skLineSegment(sketch, "E22.1.0.12", {"start": v(-22.23, 0) * mm, "end": v(-38.1, -6.76) * mm});
            skLineSegment(sketch, "E22.1.0.13", {"start": v(-38.1, 6.76) * mm, "end": v(-22.23, 0) * mm});
            skLineSegment(sketch, "E22.1.0.14", {"start": v(-53.98, 0) * mm, "end": v(-38.1, 6.76) * mm});
            skLineSegment(sketch, "E22.1.0.15", {"start": v(-22.23, -56.77) * mm, "end": v(-38.1, -63.53) * mm});
            skLineSegment(sketch, "E22.1.0.16", {"start": v(-38.1, 63.53) * mm, "end": v(-22.23, 56.77) * mm});
            skLineSegment(sketch, "E22.1.0.17", {"start": v(-38.1, 50) * mm, "end": v(-53.98, 56.77) * mm});
            skLineSegment(sketch, "E22.1.0.18", {"start": v(-22.23, 56.77) * mm, "end": v(-38.1, 50) * mm});
            skLineSegment(sketch, "E22.1.0.19", {"start": v(-22.23, 94.62) * mm, "end": v(-38.1, 87.85) * mm});
            skLineSegment(sketch, "E22.1.0.20", {"start": v(-38.1, -63.53) * mm, "end": v(-53.98, -56.77) * mm});
            skLineSegment(sketch, "E22.1.0.21", {"start": v(-53.98, 94.62) * mm, "end": v(-38.1, 101.38) * mm});
            skLineSegment(sketch, "E22.1.0.22", {"start": v(-38.1, 82.45) * mm, "end": v(-22.23, 75.7) * mm});
            skLineSegment(sketch, "E22.1.0.23", {"start": v(-38.1, 68.93) * mm, "end": v(-53.98, 75.7) * mm});
            skLineSegment(sketch, "E22.1.0.24", {"start": v(-53.98, -37.85) * mm, "end": v(-38.1, -31.08) * mm});
            skLineSegment(sketch, "E22.1.0.25", {"start": v(-22.23, 75.7) * mm, "end": v(-38.1, 68.93) * mm});
            skLineSegment(sketch, "E22.1.0.26", {"start": v(-53.98, -94.62) * mm, "end": v(-38.1, -87.85) * mm});
            skLineSegment(sketch, "E22.1.0.27", {"start": v(-38.1, -31.08) * mm, "end": v(-22.23, -37.85) * mm});
            skLineSegment(sketch, "E22.1.0.28", {"start": v(-38.1, -87.85) * mm, "end": v(-22.23, -94.62) * mm});
            skLineSegment(sketch, "E22.1.0.29", {"start": v(-22.23, -37.85) * mm, "end": v(-38.1, -44.6) * mm});
            skLineSegment(sketch, "E22.1.0.30", {"start": v(-53.98, 75.7) * mm, "end": v(-38.1, 82.45) * mm});
            skLineSegment(sketch, "E22.1.0.31", {"start": v(-22.23, -94.62) * mm, "end": v(-38.1, -101.38) * mm});
            skLineSegment(sketch, "E22.1.0.32", {"start": v(-38.1, -44.6) * mm, "end": v(-53.98, -37.85) * mm});
            skLineSegment(sketch, "E22.1.0.33", {"start": v(-22.23, -75.7) * mm, "end": v(-38.1, -82.45) * mm});
            skLineSegment(sketch, "E22.1.0.34", {"start": v(-38.1, -25.69) * mm, "end": v(-53.98, -18.92) * mm});
            skLineSegment(sketch, "E22.1.0.35", {"start": v(-38.1, -101.38) * mm, "end": v(-53.98, -94.61) * mm});
            skLineSegment(sketch, "E22.1.0.36", {"start": v(-38.1, -82.45) * mm, "end": v(-53.98, -75.7) * mm});
            skLineSegment(sketch, "E22.1.0.37", {"start": v(-53.98, -75.7) * mm, "end": v(-38.1, -68.93) * mm});
            skLineSegment(sketch, "E22.1.0.38", {"start": v(-38.1, -12.16) * mm, "end": v(-22.23, -18.92) * mm});
            skLineSegment(sketch, "E22.1.0.39", {"start": v(-53.98, -18.92) * mm, "end": v(-38.1, -12.16) * mm});
            skLineSegment(sketch, "E22.1.0.40", {"start": v(-53.98, -56.77) * mm, "end": v(-38.1, -50) * mm});
            skLineSegment(sketch, "E22.1.0.41", {"start": v(-38.1, 101.38) * mm, "end": v(-22.23, 94.62) * mm});
            skLineSegment(sketch, "E22.1.0.42", {"start": v(-22.23, -18.92) * mm, "end": v(-38.1, -25.69) * mm});
            skLineSegment(sketch, "E22.1.0.43", {"start": v(-38.1, -68.93) * mm, "end": v(-22.23, -75.7) * mm});
            skLineSegment(sketch, "E22.2.0.0", {"start": v(-76.2, -50) * mm, "end": v(-60.33, -56.77) * mm});
            skLineSegment(sketch, "E22.2.0.1", {"start": v(-76.2, 87.85) * mm, "end": v(-92.08, 94.62) * mm});
            skLineSegment(sketch, "E22.2.0.2", {"start": v(-92.08, 56.77) * mm, "end": v(-76.2, 63.53) * mm});
            skLineSegment(sketch, "E22.2.0.3", {"start": v(-76.2, 44.6) * mm, "end": v(-60.33, 37.85) * mm});
            skLineSegment(sketch, "E22.2.0.4", {"start": v(-76.2, 31.08) * mm, "end": v(-92.08, 37.85) * mm});
            skLineSegment(sketch, "E22.2.0.5", {"start": v(-60.33, 37.85) * mm, "end": v(-76.2, 31.08) * mm});
            skLineSegment(sketch, "E22.2.0.6", {"start": v(-92.08, 37.85) * mm, "end": v(-76.2, 44.6) * mm});
            skLineSegment(sketch, "E22.2.0.7", {"start": v(-76.2, 25.69) * mm, "end": v(-60.33, 18.92) * mm});
            skLineSegment(sketch, "E22.2.0.8", {"start": v(-76.2, 12.16) * mm, "end": v(-92.08, 18.92) * mm});
            skLineSegment(sketch, "E22.2.0.9", {"start": v(-60.33, 18.92) * mm, "end": v(-76.2, 12.16) * mm});
            skLineSegment(sketch, "E22.2.0.10", {"start": v(-92.08, 18.92) * mm, "end": v(-76.2, 25.69) * mm});
            skLineSegment(sketch, "E22.2.0.11", {"start": v(-76.2, -6.76) * mm, "end": v(-92.08, 0) * mm});
            skLineSegment(sketch, "E22.2.0.12", {"start": v(-60.33, 0) * mm, "end": v(-76.2, -6.76) * mm});
            skLineSegment(sketch, "E22.2.0.13", {"start": v(-76.2, 6.76) * mm, "end": v(-60.33, 0) * mm});
            skLineSegment(sketch, "E22.2.0.14", {"start": v(-92.08, 0) * mm, "end": v(-76.2, 6.76) * mm});
            skLineSegment(sketch, "E22.2.0.15", {"start": v(-60.33, -56.77) * mm, "end": v(-76.2, -63.53) * mm});
            skLineSegment(sketch, "E22.2.0.16", {"start": v(-76.2, 63.53) * mm, "end": v(-60.33, 56.77) * mm});
            skLineSegment(sketch, "E22.2.0.17", {"start": v(-76.2, 50) * mm, "end": v(-92.08, 56.77) * mm});
            skLineSegment(sketch, "E22.2.0.18", {"start": v(-60.33, 56.77) * mm, "end": v(-76.2, 50) * mm});
            skLineSegment(sketch, "E22.2.0.19", {"start": v(-60.33, 94.62) * mm, "end": v(-76.2, 87.85) * mm});
            skLineSegment(sketch, "E22.2.0.20", {"start": v(-76.2, -63.53) * mm, "end": v(-92.08, -56.77) * mm});
            skLineSegment(sketch, "E22.2.0.21", {"start": v(-92.08, 94.62) * mm, "end": v(-76.2, 101.38) * mm});
            skLineSegment(sketch, "E22.2.0.22", {"start": v(-76.2, 82.45) * mm, "end": v(-60.33, 75.7) * mm});
            skLineSegment(sketch, "E22.2.0.23", {"start": v(-76.2, 68.93) * mm, "end": v(-92.08, 75.7) * mm});
            skLineSegment(sketch, "E22.2.0.24", {"start": v(-92.08, -37.85) * mm, "end": v(-76.2, -31.08) * mm});
            skLineSegment(sketch, "E22.2.0.25", {"start": v(-60.33, 75.7) * mm, "end": v(-76.2, 68.93) * mm});
            skLineSegment(sketch, "E22.2.0.26", {"start": v(-92.08, -94.62) * mm, "end": v(-76.2, -87.85) * mm});
            skLineSegment(sketch, "E22.2.0.27", {"start": v(-76.2, -31.08) * mm, "end": v(-60.33, -37.85) * mm});
            skLineSegment(sketch, "E22.2.0.28", {"start": v(-76.2, -87.85) * mm, "end": v(-60.33, -94.62) * mm});
            skLineSegment(sketch, "E22.2.0.29", {"start": v(-60.33, -37.85) * mm, "end": v(-76.2, -44.6) * mm});
            skLineSegment(sketch, "E22.2.0.30", {"start": v(-92.08, 75.7) * mm, "end": v(-76.2, 82.45) * mm});
            skLineSegment(sketch, "E22.2.0.31", {"start": v(-60.33, -94.62) * mm, "end": v(-76.2, -101.38) * mm});
            skLineSegment(sketch, "E22.2.0.32", {"start": v(-76.2, -44.6) * mm, "end": v(-92.08, -37.85) * mm});
            skLineSegment(sketch, "E22.2.0.33", {"start": v(-60.33, -75.7) * mm, "end": v(-76.2, -82.45) * mm});
            skLineSegment(sketch, "E22.2.0.34", {"start": v(-76.2, -25.69) * mm, "end": v(-92.08, -18.92) * mm});
            skLineSegment(sketch, "E22.2.0.35", {"start": v(-76.2, -101.38) * mm, "end": v(-92.08, -94.61) * mm});
            skLineSegment(sketch, "E22.2.0.36", {"start": v(-76.2, -82.45) * mm, "end": v(-92.08, -75.7) * mm});
            skLineSegment(sketch, "E22.2.0.37", {"start": v(-92.08, -75.7) * mm, "end": v(-76.2, -68.93) * mm});
            skLineSegment(sketch, "E22.2.0.38", {"start": v(-76.2, -12.16) * mm, "end": v(-60.33, -18.92) * mm});
            skLineSegment(sketch, "E22.2.0.39", {"start": v(-92.08, -18.92) * mm, "end": v(-76.2, -12.16) * mm});
            skLineSegment(sketch, "E22.2.0.40", {"start": v(-92.08, -56.77) * mm, "end": v(-76.2, -50) * mm});
            skLineSegment(sketch, "E22.2.0.41", {"start": v(-76.2, 101.38) * mm, "end": v(-60.33, 94.62) * mm});
            skLineSegment(sketch, "E22.2.0.42", {"start": v(-60.33, -18.92) * mm, "end": v(-76.2, -25.69) * mm});
            skLineSegment(sketch, "E22.2.0.43", {"start": v(-76.2, -68.93) * mm, "end": v(-60.33, -75.7) * mm});
            skLineSegment(sketch, "E22.3.0.0", {"start": v(-114.3, -50) * mm, "end": v(-98.43, -56.77) * mm});
            skLineSegment(sketch, "E22.3.0.1", {"start": v(-114.3, 87.85) * mm, "end": v(-130.18, 94.62) * mm});
            skLineSegment(sketch, "E22.3.0.2", {"start": v(-130.18, 56.77) * mm, "end": v(-114.3, 63.53) * mm});
            skLineSegment(sketch, "E22.3.0.3", {"start": v(-114.3, 44.6) * mm, "end": v(-98.43, 37.85) * mm});
            skLineSegment(sketch, "E22.3.0.4", {"start": v(-114.3, 31.08) * mm, "end": v(-130.18, 37.85) * mm});
            skLineSegment(sketch, "E22.3.0.5", {"start": v(-98.43, 37.85) * mm, "end": v(-114.3, 31.08) * mm});
            skLineSegment(sketch, "E22.3.0.6", {"start": v(-130.18, 37.85) * mm, "end": v(-114.3, 44.6) * mm});
            skLineSegment(sketch, "E22.3.0.7", {"start": v(-114.3, 25.69) * mm, "end": v(-98.43, 18.92) * mm});
            skLineSegment(sketch, "E22.3.0.8", {"start": v(-114.3, 12.16) * mm, "end": v(-130.18, 18.92) * mm});
            skLineSegment(sketch, "E22.3.0.9", {"start": v(-98.43, 18.92) * mm, "end": v(-114.3, 12.16) * mm});
            skLineSegment(sketch, "E22.3.0.10", {"start": v(-130.18, 18.92) * mm, "end": v(-114.3, 25.69) * mm});
            skLineSegment(sketch, "E22.3.0.11", {"start": v(-114.3, -6.76) * mm, "end": v(-130.18, 0) * mm});
            skLineSegment(sketch, "E22.3.0.12", {"start": v(-98.43, 0) * mm, "end": v(-114.3, -6.76) * mm});
            skLineSegment(sketch, "E22.3.0.13", {"start": v(-114.3, 6.76) * mm, "end": v(-98.43, 0) * mm});
            skLineSegment(sketch, "E22.3.0.14", {"start": v(-130.18, 0) * mm, "end": v(-114.3, 6.76) * mm});
            skLineSegment(sketch, "E22.3.0.15", {"start": v(-98.43, -56.77) * mm, "end": v(-114.3, -63.53) * mm});
            skLineSegment(sketch, "E22.3.0.16", {"start": v(-114.3, 63.53) * mm, "end": v(-98.43, 56.77) * mm});
            skLineSegment(sketch, "E22.3.0.17", {"start": v(-114.3, 50) * mm, "end": v(-130.18, 56.77) * mm});
            skLineSegment(sketch, "E22.3.0.18", {"start": v(-98.43, 56.77) * mm, "end": v(-114.3, 50) * mm});
            skLineSegment(sketch, "E22.3.0.19", {"start": v(-98.43, 94.62) * mm, "end": v(-114.3, 87.85) * mm});
            skLineSegment(sketch, "E22.3.0.20", {"start": v(-114.3, -63.53) * mm, "end": v(-130.18, -56.77) * mm});
            skLineSegment(sketch, "E22.3.0.21", {"start": v(-130.18, 94.62) * mm, "end": v(-114.3, 101.38) * mm});
            skLineSegment(sketch, "E22.3.0.22", {"start": v(-114.3, 82.45) * mm, "end": v(-98.43, 75.7) * mm});
            skLineSegment(sketch, "E22.3.0.23", {"start": v(-114.3, 68.93) * mm, "end": v(-130.18, 75.7) * mm});
            skLineSegment(sketch, "E22.3.0.24", {"start": v(-130.18, -37.85) * mm, "end": v(-114.3, -31.08) * mm});
            skLineSegment(sketch, "E22.3.0.25", {"start": v(-98.43, 75.7) * mm, "end": v(-114.3, 68.93) * mm});
            skLineSegment(sketch, "E22.3.0.26", {"start": v(-130.18, -94.62) * mm, "end": v(-114.3, -87.85) * mm});
            skLineSegment(sketch, "E22.3.0.27", {"start": v(-114.3, -31.08) * mm, "end": v(-98.43, -37.85) * mm});
            skLineSegment(sketch, "E22.3.0.28", {"start": v(-114.3, -87.85) * mm, "end": v(-98.43, -94.62) * mm});
            skLineSegment(sketch, "E22.3.0.29", {"start": v(-98.43, -37.85) * mm, "end": v(-114.3, -44.6) * mm});
            skLineSegment(sketch, "E22.3.0.30", {"start": v(-130.18, 75.7) * mm, "end": v(-114.3, 82.45) * mm});
            skLineSegment(sketch, "E22.3.0.31", {"start": v(-98.43, -94.62) * mm, "end": v(-114.3, -101.38) * mm});
            skLineSegment(sketch, "E22.3.0.32", {"start": v(-114.3, -44.6) * mm, "end": v(-130.18, -37.85) * mm});
            skLineSegment(sketch, "E22.3.0.33", {"start": v(-98.43, -75.7) * mm, "end": v(-114.3, -82.45) * mm});
            skLineSegment(sketch, "E22.3.0.34", {"start": v(-114.3, -25.69) * mm, "end": v(-130.18, -18.92) * mm});
            skLineSegment(sketch, "E22.3.0.35", {"start": v(-114.3, -101.38) * mm, "end": v(-130.18, -94.61) * mm});
            skLineSegment(sketch, "E22.3.0.36", {"start": v(-114.3, -82.45) * mm, "end": v(-130.18, -75.7) * mm});
            skLineSegment(sketch, "E22.3.0.37", {"start": v(-130.18, -75.7) * mm, "end": v(-114.3, -68.93) * mm});
            skLineSegment(sketch, "E22.3.0.38", {"start": v(-114.3, -12.16) * mm, "end": v(-98.43, -18.92) * mm});
            skLineSegment(sketch, "E22.3.0.39", {"start": v(-130.18, -18.92) * mm, "end": v(-114.3, -12.16) * mm});
            skLineSegment(sketch, "E22.3.0.40", {"start": v(-130.18, -56.77) * mm, "end": v(-114.3, -50) * mm});
            skLineSegment(sketch, "E22.3.0.41", {"start": v(-114.3, 101.38) * mm, "end": v(-98.43, 94.62) * mm});
            skLineSegment(sketch, "E22.3.0.42", {"start": v(-98.43, -18.92) * mm, "end": v(-114.3, -25.69) * mm});
            skLineSegment(sketch, "E22.3.0.43", {"start": v(-114.3, -68.93) * mm, "end": v(-98.43, -75.7) * mm});
            skLineSegment(sketch, "E22.4.0.0", {"start": v(-152.4, -50) * mm, "end": v(-136.53, -56.77) * mm});
            skLineSegment(sketch, "E22.4.0.1", {"start": v(-152.4, 87.85) * mm, "end": v(-168.28, 94.62) * mm});
            skLineSegment(sketch, "E22.4.0.2", {"start": v(-168.28, 56.77) * mm, "end": v(-152.4, 63.53) * mm});
            skLineSegment(sketch, "E22.4.0.3", {"start": v(-152.4, 44.6) * mm, "end": v(-136.53, 37.85) * mm});
            skLineSegment(sketch, "E22.4.0.4", {"start": v(-152.4, 31.08) * mm, "end": v(-168.28, 37.85) * mm});
            skLineSegment(sketch, "E22.4.0.5", {"start": v(-136.53, 37.85) * mm, "end": v(-152.4, 31.08) * mm});
            skLineSegment(sketch, "E22.4.0.6", {"start": v(-168.28, 37.85) * mm, "end": v(-152.4, 44.6) * mm});
            skLineSegment(sketch, "E22.4.0.7", {"start": v(-152.4, 25.69) * mm, "end": v(-136.53, 18.92) * mm});
            skLineSegment(sketch, "E22.4.0.8", {"start": v(-152.4, 12.16) * mm, "end": v(-168.28, 18.92) * mm});
            skLineSegment(sketch, "E22.4.0.9", {"start": v(-136.53, 18.92) * mm, "end": v(-152.4, 12.16) * mm});
            skLineSegment(sketch, "E22.4.0.10", {"start": v(-168.28, 18.92) * mm, "end": v(-152.4, 25.69) * mm});
            skLineSegment(sketch, "E22.4.0.11", {"start": v(-152.4, -6.76) * mm, "end": v(-168.28, 0) * mm});
            skLineSegment(sketch, "E22.4.0.12", {"start": v(-136.53, 0) * mm, "end": v(-152.4, -6.76) * mm});
            skLineSegment(sketch, "E22.4.0.13", {"start": v(-152.4, 6.76) * mm, "end": v(-136.53, 0) * mm});
            skLineSegment(sketch, "E22.4.0.14", {"start": v(-168.28, 0) * mm, "end": v(-152.4, 6.76) * mm});
            skLineSegment(sketch, "E22.4.0.15", {"start": v(-136.53, -56.77) * mm, "end": v(-152.4, -63.53) * mm});
            skLineSegment(sketch, "E22.4.0.16", {"start": v(-152.4, 63.53) * mm, "end": v(-136.53, 56.77) * mm});
            skLineSegment(sketch, "E22.4.0.17", {"start": v(-152.4, 50) * mm, "end": v(-168.28, 56.77) * mm});
            skLineSegment(sketch, "E22.4.0.18", {"start": v(-136.53, 56.77) * mm, "end": v(-152.4, 50) * mm});
            skLineSegment(sketch, "E22.4.0.19", {"start": v(-136.53, 94.62) * mm, "end": v(-152.4, 87.85) * mm});
            skLineSegment(sketch, "E22.4.0.20", {"start": v(-152.4, -63.53) * mm, "end": v(-168.28, -56.77) * mm});
            skLineSegment(sketch, "E22.4.0.21", {"start": v(-168.28, 94.62) * mm, "end": v(-152.4, 101.38) * mm});
            skLineSegment(sketch, "E22.4.0.22", {"start": v(-152.4, 82.45) * mm, "end": v(-136.53, 75.7) * mm});
            skLineSegment(sketch, "E22.4.0.23", {"start": v(-152.4, 68.93) * mm, "end": v(-168.28, 75.7) * mm});
            skLineSegment(sketch, "E22.4.0.24", {"start": v(-168.28, -37.85) * mm, "end": v(-152.4, -31.08) * mm});
            skLineSegment(sketch, "E22.4.0.25", {"start": v(-136.53, 75.7) * mm, "end": v(-152.4, 68.93) * mm});
            skLineSegment(sketch, "E22.4.0.26", {"start": v(-168.28, -94.62) * mm, "end": v(-152.4, -87.85) * mm});
            skLineSegment(sketch, "E22.4.0.27", {"start": v(-152.4, -31.08) * mm, "end": v(-136.53, -37.85) * mm});
            skLineSegment(sketch, "E22.4.0.28", {"start": v(-152.4, -87.85) * mm, "end": v(-136.53, -94.62) * mm});
            skLineSegment(sketch, "E22.4.0.29", {"start": v(-136.53, -37.85) * mm, "end": v(-152.4, -44.6) * mm});
            skLineSegment(sketch, "E22.4.0.30", {"start": v(-168.28, 75.7) * mm, "end": v(-152.4, 82.45) * mm});
            skLineSegment(sketch, "E22.4.0.31", {"start": v(-136.53, -94.62) * mm, "end": v(-152.4, -101.38) * mm});
            skLineSegment(sketch, "E22.4.0.32", {"start": v(-152.4, -44.6) * mm, "end": v(-168.28, -37.85) * mm});
            skLineSegment(sketch, "E22.4.0.33", {"start": v(-136.53, -75.7) * mm, "end": v(-152.4, -82.45) * mm});
            skLineSegment(sketch, "E22.4.0.34", {"start": v(-152.4, -25.69) * mm, "end": v(-168.28, -18.92) * mm});
            skLineSegment(sketch, "E22.4.0.35", {"start": v(-152.4, -101.38) * mm, "end": v(-168.28, -94.61) * mm});
            skLineSegment(sketch, "E22.4.0.36", {"start": v(-152.4, -82.45) * mm, "end": v(-168.28, -75.7) * mm});
            skLineSegment(sketch, "E22.4.0.37", {"start": v(-168.28, -75.7) * mm, "end": v(-152.4, -68.93) * mm});
            skLineSegment(sketch, "E22.4.0.38", {"start": v(-152.4, -12.16) * mm, "end": v(-136.53, -18.92) * mm});
            skLineSegment(sketch, "E22.4.0.39", {"start": v(-168.28, -18.92) * mm, "end": v(-152.4, -12.16) * mm});
            skLineSegment(sketch, "E22.4.0.40", {"start": v(-168.28, -56.77) * mm, "end": v(-152.4, -50) * mm});
            skLineSegment(sketch, "E22.4.0.41", {"start": v(-152.4, 101.38) * mm, "end": v(-136.53, 94.62) * mm});
            skLineSegment(sketch, "E22.4.0.42", {"start": v(-136.53, -18.92) * mm, "end": v(-152.4, -25.69) * mm});
            skLineSegment(sketch, "E22.4.0.43", {"start": v(-152.4, -68.93) * mm, "end": v(-136.53, -75.7) * mm});
            skLineSegment(sketch, "E22.direction1", {"start": v(-15.88, -94.62) * mm, "end": v(-53.98, -94.62) * mm, "construction": true});
            skLineSegment(sketch, "E23", {"start": v(155.57, -85.15) * mm, "end": v(171.45, -78.4) * mm});
            skLineSegment(sketch, "E24", {"start": v(171.45, -78.4) * mm, "end": v(187.32, -85.15) * mm});
            skLineSegment(sketch, "E25", {"start": v(187.32, -85.15) * mm, "end": v(171.45, -91.92) * mm});
            skLineSegment(sketch, "E26", {"start": v(171.45, -91.92) * mm, "end": v(155.57, -85.15) * mm});
            skLineSegment(sketch, "E27.0.1.0", {"start": v(171.45, -73) * mm, "end": v(155.57, -66.23) * mm});
            skLineSegment(sketch, "E27.0.1.1", {"start": v(155.57, -66.23) * mm, "end": v(171.45, -59.47) * mm});
            skLineSegment(sketch, "E27.0.1.2", {"start": v(171.45, -59.47) * mm, "end": v(187.32, -66.23) * mm});
            skLineSegment(sketch, "E27.0.1.3", {"start": v(187.32, -66.23) * mm, "end": v(171.45, -73) * mm});
            skLineSegment(sketch, "E27.0.2.0", {"start": v(171.45, -54.07) * mm, "end": v(155.57, -47.3) * mm});
            skLineSegment(sketch, "E27.0.2.1", {"start": v(155.57, -47.3) * mm, "end": v(171.45, -40.54) * mm});
            skLineSegment(sketch, "E27.0.2.2", {"start": v(171.45, -40.54) * mm, "end": v(187.32, -47.3) * mm});
            skLineSegment(sketch, "E27.0.2.3", {"start": v(187.32, -47.3) * mm, "end": v(171.45, -54.07) * mm});
            skLineSegment(sketch, "E27.0.3.0", {"start": v(171.45, -35.15) * mm, "end": v(155.57, -28.38) * mm});
            skLineSegment(sketch, "E27.0.3.1", {"start": v(155.57, -28.38) * mm, "end": v(171.45, -21.62) * mm});
            skLineSegment(sketch, "E27.0.3.2", {"start": v(171.45, -21.62) * mm, "end": v(187.32, -28.38) * mm});
            skLineSegment(sketch, "E27.0.3.3", {"start": v(187.32, -28.38) * mm, "end": v(171.45, -35.15) * mm});
            skLineSegment(sketch, "E27.0.4.0", {"start": v(171.45, -16.22) * mm, "end": v(155.57, -9.46) * mm});
            skLineSegment(sketch, "E27.0.4.1", {"start": v(155.57, -9.46) * mm, "end": v(171.45, -2.7) * mm});
            skLineSegment(sketch, "E27.0.4.2", {"start": v(171.45, -2.7) * mm, "end": v(187.32, -9.46) * mm});
            skLineSegment(sketch, "E27.0.4.3", {"start": v(187.32, -9.46) * mm, "end": v(171.45, -16.22) * mm});
            skLineSegment(sketch, "E27.0.5.0", {"start": v(171.45, 2.7) * mm, "end": v(155.57, 9.46) * mm});
            skLineSegment(sketch, "E27.0.5.1", {"start": v(155.57, 9.46) * mm, "end": v(171.45, 16.22) * mm});
            skLineSegment(sketch, "E27.0.5.2", {"start": v(171.45, 16.22) * mm, "end": v(187.32, 9.46) * mm});
            skLineSegment(sketch, "E27.0.5.3", {"start": v(187.32, 9.46) * mm, "end": v(171.45, 2.7) * mm});
            skLineSegment(sketch, "E27.0.6.0", {"start": v(171.45, 21.62) * mm, "end": v(155.57, 28.38) * mm});
            skLineSegment(sketch, "E27.0.6.1", {"start": v(155.57, 28.38) * mm, "end": v(171.45, 35.15) * mm});
            skLineSegment(sketch, "E27.0.6.2", {"start": v(171.45, 35.15) * mm, "end": v(187.32, 28.38) * mm});
            skLineSegment(sketch, "E27.0.6.3", {"start": v(187.32, 28.38) * mm, "end": v(171.45, 21.62) * mm});
            skLineSegment(sketch, "E27.0.7.0", {"start": v(171.45, 40.54) * mm, "end": v(155.57, 47.3) * mm});
            skLineSegment(sketch, "E27.0.7.1", {"start": v(155.57, 47.3) * mm, "end": v(171.45, 54.07) * mm});
            skLineSegment(sketch, "E27.0.7.2", {"start": v(171.45, 54.07) * mm, "end": v(187.32, 47.3) * mm});
            skLineSegment(sketch, "E27.0.7.3", {"start": v(187.32, 47.3) * mm, "end": v(171.45, 40.54) * mm});
            skLineSegment(sketch, "E27.0.8.0", {"start": v(171.45, 59.47) * mm, "end": v(155.57, 66.23) * mm});
            skLineSegment(sketch, "E27.0.8.1", {"start": v(155.57, 66.23) * mm, "end": v(171.45, 73) * mm});
            skLineSegment(sketch, "E27.0.8.2", {"start": v(171.45, 73) * mm, "end": v(187.32, 66.23) * mm});
            skLineSegment(sketch, "E27.0.8.3", {"start": v(187.32, 66.23) * mm, "end": v(171.45, 59.47) * mm});
            skLineSegment(sketch, "E27.0.9.0", {"start": v(171.45, 78.4) * mm, "end": v(155.57, 85.15) * mm});
            skLineSegment(sketch, "E27.0.9.1", {"start": v(155.57, 85.15) * mm, "end": v(171.45, 91.92) * mm});
            skLineSegment(sketch, "E27.0.9.2", {"start": v(171.45, 91.92) * mm, "end": v(187.32, 85.15) * mm});
            skLineSegment(sketch, "E27.0.9.3", {"start": v(187.32, 85.15) * mm, "end": v(171.45, 78.4) * mm});
            skLineSegment(sketch, "E27.1.0.0", {"start": v(133.35, -91.92) * mm, "end": v(117.47, -85.15) * mm});
            skLineSegment(sketch, "E27.1.0.1", {"start": v(117.47, -85.15) * mm, "end": v(133.35, -78.4) * mm});
            skLineSegment(sketch, "E27.1.0.2", {"start": v(133.35, -78.4) * mm, "end": v(149.22, -85.15) * mm});
            skLineSegment(sketch, "E27.1.0.3", {"start": v(149.22, -85.15) * mm, "end": v(133.35, -91.92) * mm});
            skLineSegment(sketch, "E27.1.1.0", {"start": v(133.35, -73) * mm, "end": v(117.47, -66.23) * mm});
            skLineSegment(sketch, "E27.1.1.1", {"start": v(117.47, -66.23) * mm, "end": v(133.35, -59.47) * mm});
            skLineSegment(sketch, "E27.1.1.2", {"start": v(133.35, -59.47) * mm, "end": v(149.22, -66.23) * mm});
            skLineSegment(sketch, "E27.1.1.3", {"start": v(149.22, -66.23) * mm, "end": v(133.35, -73) * mm});
            skLineSegment(sketch, "E27.1.2.0", {"start": v(133.35, -54.07) * mm, "end": v(117.47, -47.3) * mm});
            skLineSegment(sketch, "E27.1.2.1", {"start": v(117.47, -47.3) * mm, "end": v(133.35, -40.54) * mm});
            skLineSegment(sketch, "E27.1.2.2", {"start": v(133.35, -40.54) * mm, "end": v(149.22, -47.3) * mm});
            skLineSegment(sketch, "E27.1.2.3", {"start": v(149.22, -47.3) * mm, "end": v(133.35, -54.07) * mm});
            skLineSegment(sketch, "E27.1.3.0", {"start": v(133.35, -35.15) * mm, "end": v(117.47, -28.38) * mm});
            skLineSegment(sketch, "E27.1.3.1", {"start": v(117.47, -28.38) * mm, "end": v(133.35, -21.62) * mm});
            skLineSegment(sketch, "E27.1.3.2", {"start": v(133.35, -21.62) * mm, "end": v(149.22, -28.38) * mm});
            skLineSegment(sketch, "E27.1.3.3", {"start": v(149.22, -28.38) * mm, "end": v(133.35, -35.15) * mm});
            skLineSegment(sketch, "E27.1.4.0", {"start": v(133.35, -16.22) * mm, "end": v(117.47, -9.46) * mm});
            skLineSegment(sketch, "E27.1.4.1", {"start": v(117.47, -9.46) * mm, "end": v(133.35, -2.7) * mm});
            skLineSegment(sketch, "E27.1.4.2", {"start": v(133.35, -2.7) * mm, "end": v(149.22, -9.46) * mm});
            skLineSegment(sketch, "E27.1.4.3", {"start": v(149.22, -9.46) * mm, "end": v(133.35, -16.22) * mm});
            skLineSegment(sketch, "E27.1.5.0", {"start": v(133.35, 2.7) * mm, "end": v(117.47, 9.46) * mm});
            skLineSegment(sketch, "E27.1.5.1", {"start": v(117.47, 9.46) * mm, "end": v(133.35, 16.22) * mm});
            skLineSegment(sketch, "E27.1.5.2", {"start": v(133.35, 16.22) * mm, "end": v(149.22, 9.46) * mm});
            skLineSegment(sketch, "E27.1.5.3", {"start": v(149.22, 9.46) * mm, "end": v(133.35, 2.7) * mm});
            skLineSegment(sketch, "E27.1.6.0", {"start": v(133.35, 21.62) * mm, "end": v(117.47, 28.38) * mm});
            skLineSegment(sketch, "E27.1.6.1", {"start": v(117.47, 28.38) * mm, "end": v(133.35, 35.15) * mm});
            skLineSegment(sketch, "E27.1.6.2", {"start": v(133.35, 35.15) * mm, "end": v(149.22, 28.38) * mm});
            skLineSegment(sketch, "E27.1.6.3", {"start": v(149.22, 28.38) * mm, "end": v(133.35, 21.62) * mm});
            skLineSegment(sketch, "E27.1.7.0", {"start": v(133.35, 40.54) * mm, "end": v(117.47, 47.3) * mm});
            skLineSegment(sketch, "E27.1.7.1", {"start": v(117.47, 47.3) * mm, "end": v(133.35, 54.07) * mm});
            skLineSegment(sketch, "E27.1.7.2", {"start": v(133.35, 54.07) * mm, "end": v(149.22, 47.3) * mm});
            skLineSegment(sketch, "E27.1.7.3", {"start": v(149.22, 47.3) * mm, "end": v(133.35, 40.54) * mm});
            skLineSegment(sketch, "E27.1.8.0", {"start": v(133.35, 59.47) * mm, "end": v(117.47, 66.23) * mm});
            skLineSegment(sketch, "E27.1.8.1", {"start": v(117.47, 66.23) * mm, "end": v(133.35, 73) * mm});
            skLineSegment(sketch, "E27.1.8.2", {"start": v(133.35, 73) * mm, "end": v(149.22, 66.23) * mm});
            skLineSegment(sketch, "E27.1.8.3", {"start": v(149.22, 66.23) * mm, "end": v(133.35, 59.47) * mm});
            skLineSegment(sketch, "E27.1.9.0", {"start": v(133.35, 78.4) * mm, "end": v(117.47, 85.15) * mm});
            skLineSegment(sketch, "E27.1.9.1", {"start": v(117.47, 85.15) * mm, "end": v(133.35, 91.92) * mm});
            skLineSegment(sketch, "E27.1.9.2", {"start": v(133.35, 91.92) * mm, "end": v(149.22, 85.15) * mm});
            skLineSegment(sketch, "E27.1.9.3", {"start": v(149.22, 85.15) * mm, "end": v(133.35, 78.4) * mm});
            skLineSegment(sketch, "E27.2.0.0", {"start": v(95.25, -91.92) * mm, "end": v(79.37, -85.15) * mm});
            skLineSegment(sketch, "E27.2.0.1", {"start": v(79.37, -85.15) * mm, "end": v(95.25, -78.4) * mm});
            skLineSegment(sketch, "E27.2.0.2", {"start": v(95.25, -78.4) * mm, "end": v(111.12, -85.15) * mm});
            skLineSegment(sketch, "E27.2.0.3", {"start": v(111.12, -85.15) * mm, "end": v(95.25, -91.92) * mm});
            skLineSegment(sketch, "E27.2.1.0", {"start": v(95.25, -73) * mm, "end": v(79.37, -66.23) * mm});
            skLineSegment(sketch, "E27.2.1.1", {"start": v(79.37, -66.23) * mm, "end": v(95.25, -59.47) * mm});
            skLineSegment(sketch, "E27.2.1.2", {"start": v(95.25, -59.47) * mm, "end": v(111.12, -66.23) * mm});
            skLineSegment(sketch, "E27.2.1.3", {"start": v(111.12, -66.23) * mm, "end": v(95.25, -73) * mm});
            skLineSegment(sketch, "E27.2.2.0", {"start": v(95.25, -54.07) * mm, "end": v(79.37, -47.3) * mm});
            skLineSegment(sketch, "E27.2.2.1", {"start": v(79.37, -47.3) * mm, "end": v(95.25, -40.54) * mm});
            skLineSegment(sketch, "E27.2.2.2", {"start": v(95.25, -40.54) * mm, "end": v(111.12, -47.3) * mm});
            skLineSegment(sketch, "E27.2.2.3", {"start": v(111.12, -47.3) * mm, "end": v(95.25, -54.07) * mm});
            skLineSegment(sketch, "E27.2.3.0", {"start": v(95.25, -35.15) * mm, "end": v(79.37, -28.38) * mm});
            skLineSegment(sketch, "E27.2.3.1", {"start": v(79.37, -28.38) * mm, "end": v(95.25, -21.62) * mm});
            skLineSegment(sketch, "E27.2.3.2", {"start": v(95.25, -21.62) * mm, "end": v(111.12, -28.38) * mm});
            skLineSegment(sketch, "E27.2.3.3", {"start": v(111.12, -28.38) * mm, "end": v(95.25, -35.15) * mm});
            skLineSegment(sketch, "E27.2.4.0", {"start": v(95.25, -16.22) * mm, "end": v(79.37, -9.46) * mm});
            skLineSegment(sketch, "E27.2.4.1", {"start": v(79.37, -9.46) * mm, "end": v(95.25, -2.7) * mm});
            skLineSegment(sketch, "E27.2.4.2", {"start": v(95.25, -2.7) * mm, "end": v(111.12, -9.46) * mm});
            skLineSegment(sketch, "E27.2.4.3", {"start": v(111.12, -9.46) * mm, "end": v(95.25, -16.22) * mm});
            skLineSegment(sketch, "E27.2.5.0", {"start": v(95.25, 2.7) * mm, "end": v(79.37, 9.46) * mm});
            skLineSegment(sketch, "E27.2.5.1", {"start": v(79.37, 9.46) * mm, "end": v(95.25, 16.22) * mm});
            skLineSegment(sketch, "E27.2.5.2", {"start": v(95.25, 16.22) * mm, "end": v(111.12, 9.46) * mm});
            skLineSegment(sketch, "E27.2.5.3", {"start": v(111.12, 9.46) * mm, "end": v(95.25, 2.7) * mm});
            skLineSegment(sketch, "E27.2.6.0", {"start": v(95.25, 21.62) * mm, "end": v(79.37, 28.38) * mm});
            skLineSegment(sketch, "E27.2.6.1", {"start": v(79.37, 28.38) * mm, "end": v(95.25, 35.15) * mm});
            skLineSegment(sketch, "E27.2.6.2", {"start": v(95.25, 35.15) * mm, "end": v(111.12, 28.38) * mm});
            skLineSegment(sketch, "E27.2.6.3", {"start": v(111.12, 28.38) * mm, "end": v(95.25, 21.62) * mm});
            skLineSegment(sketch, "E27.2.7.0", {"start": v(95.25, 40.54) * mm, "end": v(79.37, 47.3) * mm});
            skLineSegment(sketch, "E27.2.7.1", {"start": v(79.37, 47.3) * mm, "end": v(95.25, 54.07) * mm});
            skLineSegment(sketch, "E27.2.7.2", {"start": v(95.25, 54.07) * mm, "end": v(111.12, 47.3) * mm});
            skLineSegment(sketch, "E27.2.7.3", {"start": v(111.12, 47.3) * mm, "end": v(95.25, 40.54) * mm});
            skLineSegment(sketch, "E27.2.8.0", {"start": v(95.25, 59.47) * mm, "end": v(79.37, 66.23) * mm});
            skLineSegment(sketch, "E27.2.8.1", {"start": v(79.37, 66.23) * mm, "end": v(95.25, 73) * mm});
            skLineSegment(sketch, "E27.2.8.2", {"start": v(95.25, 73) * mm, "end": v(111.12, 66.23) * mm});
            skLineSegment(sketch, "E27.2.8.3", {"start": v(111.12, 66.23) * mm, "end": v(95.25, 59.47) * mm});
            skLineSegment(sketch, "E27.2.9.0", {"start": v(95.25, 78.4) * mm, "end": v(79.37, 85.15) * mm});
            skLineSegment(sketch, "E27.2.9.1", {"start": v(79.37, 85.15) * mm, "end": v(95.25, 91.92) * mm});
            skLineSegment(sketch, "E27.2.9.2", {"start": v(95.25, 91.92) * mm, "end": v(111.12, 85.15) * mm});
            skLineSegment(sketch, "E27.2.9.3", {"start": v(111.12, 85.15) * mm, "end": v(95.25, 78.4) * mm});
            skLineSegment(sketch, "E27.3.0.0", {"start": v(57.15, -91.92) * mm, "end": v(41.27, -85.15) * mm});
            skLineSegment(sketch, "E27.3.0.1", {"start": v(41.27, -85.15) * mm, "end": v(57.15, -78.4) * mm});
            skLineSegment(sketch, "E27.3.0.2", {"start": v(57.15, -78.4) * mm, "end": v(73.02, -85.15) * mm});
            skLineSegment(sketch, "E27.3.0.3", {"start": v(73.02, -85.15) * mm, "end": v(57.15, -91.92) * mm});
            skLineSegment(sketch, "E27.3.1.0", {"start": v(57.15, -73) * mm, "end": v(41.27, -66.23) * mm});
            skLineSegment(sketch, "E27.3.1.1", {"start": v(41.27, -66.23) * mm, "end": v(57.15, -59.47) * mm});
            skLineSegment(sketch, "E27.3.1.2", {"start": v(57.15, -59.47) * mm, "end": v(73.02, -66.23) * mm});
            skLineSegment(sketch, "E27.3.1.3", {"start": v(73.02, -66.23) * mm, "end": v(57.15, -73) * mm});
            skLineSegment(sketch, "E27.3.2.0", {"start": v(57.15, -54.07) * mm, "end": v(41.27, -47.3) * mm});
            skLineSegment(sketch, "E27.3.2.1", {"start": v(41.27, -47.3) * mm, "end": v(57.15, -40.54) * mm});
            skLineSegment(sketch, "E27.3.2.2", {"start": v(57.15, -40.54) * mm, "end": v(73.02, -47.3) * mm});
            skLineSegment(sketch, "E27.3.2.3", {"start": v(73.02, -47.3) * mm, "end": v(57.15, -54.07) * mm});
            skLineSegment(sketch, "E27.3.3.0", {"start": v(57.15, -35.15) * mm, "end": v(41.27, -28.38) * mm});
            skLineSegment(sketch, "E27.3.3.1", {"start": v(41.27, -28.38) * mm, "end": v(57.15, -21.62) * mm});
            skLineSegment(sketch, "E27.3.3.2", {"start": v(57.15, -21.62) * mm, "end": v(73.02, -28.38) * mm});
            skLineSegment(sketch, "E27.3.3.3", {"start": v(73.02, -28.38) * mm, "end": v(57.15, -35.15) * mm});
            skLineSegment(sketch, "E27.3.4.0", {"start": v(57.15, -16.22) * mm, "end": v(41.27, -9.46) * mm});
            skLineSegment(sketch, "E27.3.4.1", {"start": v(41.27, -9.46) * mm, "end": v(57.15, -2.7) * mm});
            skLineSegment(sketch, "E27.3.4.2", {"start": v(57.15, -2.7) * mm, "end": v(73.02, -9.46) * mm});
            skLineSegment(sketch, "E27.3.4.3", {"start": v(73.02, -9.46) * mm, "end": v(57.15, -16.22) * mm});
            skLineSegment(sketch, "E27.3.5.0", {"start": v(57.15, 2.7) * mm, "end": v(41.27, 9.46) * mm});
            skLineSegment(sketch, "E27.3.5.1", {"start": v(41.27, 9.46) * mm, "end": v(57.15, 16.22) * mm});
            skLineSegment(sketch, "E27.3.5.2", {"start": v(57.15, 16.22) * mm, "end": v(73.02, 9.46) * mm});
            skLineSegment(sketch, "E27.3.5.3", {"start": v(73.02, 9.46) * mm, "end": v(57.15, 2.7) * mm});
            skLineSegment(sketch, "E27.3.6.0", {"start": v(57.15, 21.62) * mm, "end": v(41.27, 28.38) * mm});
            skLineSegment(sketch, "E27.3.6.1", {"start": v(41.27, 28.38) * mm, "end": v(57.15, 35.15) * mm});
            skLineSegment(sketch, "E27.3.6.2", {"start": v(57.15, 35.15) * mm, "end": v(73.02, 28.38) * mm});
            skLineSegment(sketch, "E27.3.6.3", {"start": v(73.02, 28.38) * mm, "end": v(57.15, 21.62) * mm});
            skLineSegment(sketch, "E27.3.7.0", {"start": v(57.15, 40.54) * mm, "end": v(41.27, 47.3) * mm});
            skLineSegment(sketch, "E27.3.7.1", {"start": v(41.27, 47.3) * mm, "end": v(57.15, 54.07) * mm});
            skLineSegment(sketch, "E27.3.7.2", {"start": v(57.15, 54.07) * mm, "end": v(73.02, 47.3) * mm});
            skLineSegment(sketch, "E27.3.7.3", {"start": v(73.02, 47.3) * mm, "end": v(57.15, 40.54) * mm});
            skLineSegment(sketch, "E27.3.8.0", {"start": v(57.15, 59.47) * mm, "end": v(41.27, 66.23) * mm});
            skLineSegment(sketch, "E27.3.8.1", {"start": v(41.27, 66.23) * mm, "end": v(57.15, 73) * mm});
            skLineSegment(sketch, "E27.3.8.2", {"start": v(57.15, 73) * mm, "end": v(73.02, 66.23) * mm});
            skLineSegment(sketch, "E27.3.8.3", {"start": v(73.02, 66.23) * mm, "end": v(57.15, 59.47) * mm});
            skLineSegment(sketch, "E27.3.9.0", {"start": v(57.15, 78.4) * mm, "end": v(41.27, 85.15) * mm});
            skLineSegment(sketch, "E27.3.9.1", {"start": v(41.27, 85.15) * mm, "end": v(57.15, 91.92) * mm});
            skLineSegment(sketch, "E27.3.9.2", {"start": v(57.15, 91.92) * mm, "end": v(73.02, 85.15) * mm});
            skLineSegment(sketch, "E27.3.9.3", {"start": v(73.02, 85.15) * mm, "end": v(57.15, 78.4) * mm});
            skLineSegment(sketch, "E27.4.0.0", {"start": v(19.05, -91.92) * mm, "end": v(3.17, -85.15) * mm});
            skLineSegment(sketch, "E27.4.0.1", {"start": v(3.17, -85.15) * mm, "end": v(19.05, -78.4) * mm});
            skLineSegment(sketch, "E27.4.0.2", {"start": v(19.05, -78.4) * mm, "end": v(34.92, -85.15) * mm});
            skLineSegment(sketch, "E27.4.0.3", {"start": v(34.92, -85.15) * mm, "end": v(19.05, -91.92) * mm});
            skLineSegment(sketch, "E27.4.1.0", {"start": v(19.05, -73) * mm, "end": v(3.17, -66.23) * mm});
            skLineSegment(sketch, "E27.4.1.1", {"start": v(3.17, -66.23) * mm, "end": v(19.05, -59.47) * mm});
            skLineSegment(sketch, "E27.4.1.2", {"start": v(19.05, -59.47) * mm, "end": v(34.92, -66.23) * mm});
            skLineSegment(sketch, "E27.4.1.3", {"start": v(34.92, -66.23) * mm, "end": v(19.05, -73) * mm});
            skLineSegment(sketch, "E27.4.2.0", {"start": v(19.05, -54.07) * mm, "end": v(3.17, -47.3) * mm});
            skLineSegment(sketch, "E27.4.2.1", {"start": v(3.17, -47.3) * mm, "end": v(19.05, -40.54) * mm});
            skLineSegment(sketch, "E27.4.2.2", {"start": v(19.05, -40.54) * mm, "end": v(34.92, -47.3) * mm});
            skLineSegment(sketch, "E27.4.2.3", {"start": v(34.92, -47.3) * mm, "end": v(19.05, -54.07) * mm});
            skLineSegment(sketch, "E27.4.3.0", {"start": v(19.05, -35.15) * mm, "end": v(3.17, -28.38) * mm});
            skLineSegment(sketch, "E27.4.3.1", {"start": v(3.17, -28.38) * mm, "end": v(19.05, -21.62) * mm});
            skLineSegment(sketch, "E27.4.3.2", {"start": v(19.05, -21.62) * mm, "end": v(34.92, -28.38) * mm});
            skLineSegment(sketch, "E27.4.3.3", {"start": v(34.92, -28.38) * mm, "end": v(19.05, -35.15) * mm});
            skLineSegment(sketch, "E27.4.4.0", {"start": v(19.05, -16.22) * mm, "end": v(3.17, -9.46) * mm});
            skLineSegment(sketch, "E27.4.4.1", {"start": v(3.17, -9.46) * mm, "end": v(19.05, -2.7) * mm});
            skLineSegment(sketch, "E27.4.4.2", {"start": v(19.05, -2.7) * mm, "end": v(34.92, -9.46) * mm});
            skLineSegment(sketch, "E27.4.4.3", {"start": v(34.92, -9.46) * mm, "end": v(19.05, -16.22) * mm});
            skLineSegment(sketch, "E27.4.5.0", {"start": v(19.05, 2.7) * mm, "end": v(3.17, 9.46) * mm});
            skLineSegment(sketch, "E27.4.5.1", {"start": v(3.17, 9.46) * mm, "end": v(19.05, 16.22) * mm});
            skLineSegment(sketch, "E27.4.5.2", {"start": v(19.05, 16.22) * mm, "end": v(34.92, 9.46) * mm});
            skLineSegment(sketch, "E27.4.5.3", {"start": v(34.92, 9.46) * mm, "end": v(19.05, 2.7) * mm});
            skLineSegment(sketch, "E27.4.6.0", {"start": v(19.05, 21.62) * mm, "end": v(3.17, 28.38) * mm});
            skLineSegment(sketch, "E27.4.6.1", {"start": v(3.17, 28.38) * mm, "end": v(19.05, 35.15) * mm});
            skLineSegment(sketch, "E27.4.6.2", {"start": v(19.05, 35.15) * mm, "end": v(34.92, 28.38) * mm});
            skLineSegment(sketch, "E27.4.6.3", {"start": v(34.92, 28.38) * mm, "end": v(19.05, 21.62) * mm});
            skLineSegment(sketch, "E27.4.7.0", {"start": v(19.05, 40.54) * mm, "end": v(3.17, 47.3) * mm});
            skLineSegment(sketch, "E27.4.7.1", {"start": v(3.17, 47.3) * mm, "end": v(19.05, 54.07) * mm});
            skLineSegment(sketch, "E27.4.7.2", {"start": v(19.05, 54.07) * mm, "end": v(34.92, 47.3) * mm});
            skLineSegment(sketch, "E27.4.7.3", {"start": v(34.92, 47.3) * mm, "end": v(19.05, 40.54) * mm});
            skLineSegment(sketch, "E27.4.8.0", {"start": v(19.05, 59.47) * mm, "end": v(3.17, 66.23) * mm});
            skLineSegment(sketch, "E27.4.8.1", {"start": v(3.17, 66.23) * mm, "end": v(19.05, 73) * mm});
            skLineSegment(sketch, "E27.4.8.2", {"start": v(19.05, 73) * mm, "end": v(34.92, 66.23) * mm});
            skLineSegment(sketch, "E27.4.8.3", {"start": v(34.92, 66.23) * mm, "end": v(19.05, 59.47) * mm});
            skLineSegment(sketch, "E27.4.9.0", {"start": v(19.05, 78.4) * mm, "end": v(3.17, 85.15) * mm});
            skLineSegment(sketch, "E27.4.9.1", {"start": v(3.17, 85.15) * mm, "end": v(19.05, 91.92) * mm});
            skLineSegment(sketch, "E27.4.9.2", {"start": v(19.05, 91.92) * mm, "end": v(34.92, 85.15) * mm});
            skLineSegment(sketch, "E27.4.9.3", {"start": v(34.92, 85.15) * mm, "end": v(19.05, 78.4) * mm});
            skLineSegment(sketch, "E27.5.0.0", {"start": v(-19.05, -91.92) * mm, "end": v(-34.93, -85.15) * mm});
            skLineSegment(sketch, "E27.5.0.1", {"start": v(-34.93, -85.15) * mm, "end": v(-19.05, -78.4) * mm});
            skLineSegment(sketch, "E27.5.0.2", {"start": v(-19.05, -78.4) * mm, "end": v(-3.18, -85.15) * mm});
            skLineSegment(sketch, "E27.5.0.3", {"start": v(-3.18, -85.15) * mm, "end": v(-19.05, -91.92) * mm});
            skLineSegment(sketch, "E27.5.1.0", {"start": v(-19.05, -73) * mm, "end": v(-34.93, -66.23) * mm});
            skLineSegment(sketch, "E27.5.1.1", {"start": v(-34.93, -66.23) * mm, "end": v(-19.05, -59.47) * mm});
            skLineSegment(sketch, "E27.5.1.2", {"start": v(-19.05, -59.47) * mm, "end": v(-3.18, -66.23) * mm});
            skLineSegment(sketch, "E27.5.1.3", {"start": v(-3.18, -66.23) * mm, "end": v(-19.05, -73) * mm});
            skLineSegment(sketch, "E27.5.2.0", {"start": v(-19.05, -54.07) * mm, "end": v(-34.93, -47.3) * mm});
            skLineSegment(sketch, "E27.5.2.1", {"start": v(-34.93, -47.3) * mm, "end": v(-19.05, -40.54) * mm});
            skLineSegment(sketch, "E27.5.2.2", {"start": v(-19.05, -40.54) * mm, "end": v(-3.18, -47.3) * mm});
            skLineSegment(sketch, "E27.5.2.3", {"start": v(-3.18, -47.3) * mm, "end": v(-19.05, -54.07) * mm});
            skLineSegment(sketch, "E27.5.3.0", {"start": v(-19.05, -35.15) * mm, "end": v(-34.93, -28.38) * mm});
            skLineSegment(sketch, "E27.5.3.1", {"start": v(-34.93, -28.38) * mm, "end": v(-19.05, -21.62) * mm});
            skLineSegment(sketch, "E27.5.3.2", {"start": v(-19.05, -21.62) * mm, "end": v(-3.18, -28.38) * mm});
            skLineSegment(sketch, "E27.5.3.3", {"start": v(-3.18, -28.38) * mm, "end": v(-19.05, -35.15) * mm});
            skLineSegment(sketch, "E27.5.4.0", {"start": v(-19.05, -16.22) * mm, "end": v(-34.93, -9.46) * mm});
            skLineSegment(sketch, "E27.5.4.1", {"start": v(-34.93, -9.46) * mm, "end": v(-19.05, -2.7) * mm});
            skLineSegment(sketch, "E27.5.4.2", {"start": v(-19.05, -2.7) * mm, "end": v(-3.18, -9.46) * mm});
            skLineSegment(sketch, "E27.5.4.3", {"start": v(-3.18, -9.46) * mm, "end": v(-19.05, -16.22) * mm});
            skLineSegment(sketch, "E27.5.5.0", {"start": v(-19.05, 2.7) * mm, "end": v(-34.93, 9.46) * mm});
            skLineSegment(sketch, "E27.5.5.1", {"start": v(-34.93, 9.46) * mm, "end": v(-19.05, 16.22) * mm});
            skLineSegment(sketch, "E27.5.5.2", {"start": v(-19.05, 16.22) * mm, "end": v(-3.18, 9.46) * mm});
            skLineSegment(sketch, "E27.5.5.3", {"start": v(-3.18, 9.46) * mm, "end": v(-19.05, 2.7) * mm});
            skLineSegment(sketch, "E27.5.6.0", {"start": v(-19.05, 21.62) * mm, "end": v(-34.93, 28.38) * mm});
            skLineSegment(sketch, "E27.5.6.1", {"start": v(-34.93, 28.38) * mm, "end": v(-19.05, 35.15) * mm});
            skLineSegment(sketch, "E27.5.6.2", {"start": v(-19.05, 35.15) * mm, "end": v(-3.18, 28.38) * mm});
            skLineSegment(sketch, "E27.5.6.3", {"start": v(-3.18, 28.38) * mm, "end": v(-19.05, 21.62) * mm});
            skLineSegment(sketch, "E27.5.7.0", {"start": v(-19.05, 40.54) * mm, "end": v(-34.93, 47.3) * mm});
            skLineSegment(sketch, "E27.5.7.1", {"start": v(-34.93, 47.3) * mm, "end": v(-19.05, 54.07) * mm});
            skLineSegment(sketch, "E27.5.7.2", {"start": v(-19.05, 54.07) * mm, "end": v(-3.18, 47.3) * mm});
            skLineSegment(sketch, "E27.5.7.3", {"start": v(-3.18, 47.3) * mm, "end": v(-19.05, 40.54) * mm});
            skLineSegment(sketch, "E27.5.8.0", {"start": v(-19.05, 59.47) * mm, "end": v(-34.93, 66.23) * mm});
            skLineSegment(sketch, "E27.5.8.1", {"start": v(-34.93, 66.23) * mm, "end": v(-19.05, 73) * mm});
            skLineSegment(sketch, "E27.5.8.2", {"start": v(-19.05, 73) * mm, "end": v(-3.18, 66.23) * mm});
            skLineSegment(sketch, "E27.5.8.3", {"start": v(-3.18, 66.23) * mm, "end": v(-19.05, 59.47) * mm});
            skLineSegment(sketch, "E27.5.9.0", {"start": v(-19.05, 78.4) * mm, "end": v(-34.93, 85.15) * mm});
            skLineSegment(sketch, "E27.5.9.1", {"start": v(-34.93, 85.15) * mm, "end": v(-19.05, 91.92) * mm});
            skLineSegment(sketch, "E27.5.9.2", {"start": v(-19.05, 91.92) * mm, "end": v(-3.18, 85.15) * mm});
            skLineSegment(sketch, "E27.5.9.3", {"start": v(-3.18, 85.15) * mm, "end": v(-19.05, 78.4) * mm});
            skLineSegment(sketch, "E27.6.0.0", {"start": v(-57.15, -91.92) * mm, "end": v(-73.03, -85.15) * mm});
            skLineSegment(sketch, "E27.6.0.1", {"start": v(-73.03, -85.15) * mm, "end": v(-57.15, -78.4) * mm});
            skLineSegment(sketch, "E27.6.0.2", {"start": v(-57.15, -78.4) * mm, "end": v(-41.28, -85.15) * mm});
            skLineSegment(sketch, "E27.6.0.3", {"start": v(-41.28, -85.15) * mm, "end": v(-57.15, -91.92) * mm});
            skLineSegment(sketch, "E27.6.1.0", {"start": v(-57.15, -73) * mm, "end": v(-73.03, -66.23) * mm});
            skLineSegment(sketch, "E27.6.1.1", {"start": v(-73.03, -66.23) * mm, "end": v(-57.15, -59.47) * mm});
            skLineSegment(sketch, "E27.6.1.2", {"start": v(-57.15, -59.47) * mm, "end": v(-41.28, -66.23) * mm});
            skLineSegment(sketch, "E27.6.1.3", {"start": v(-41.28, -66.23) * mm, "end": v(-57.15, -73) * mm});
            skLineSegment(sketch, "E27.6.2.0", {"start": v(-57.15, -54.07) * mm, "end": v(-73.03, -47.3) * mm});
            skLineSegment(sketch, "E27.6.2.1", {"start": v(-73.03, -47.3) * mm, "end": v(-57.15, -40.54) * mm});
            skLineSegment(sketch, "E27.6.2.2", {"start": v(-57.15, -40.54) * mm, "end": v(-41.28, -47.3) * mm});
            skLineSegment(sketch, "E27.6.2.3", {"start": v(-41.28, -47.3) * mm, "end": v(-57.15, -54.07) * mm});
            skLineSegment(sketch, "E27.6.3.0", {"start": v(-57.15, -35.15) * mm, "end": v(-73.03, -28.38) * mm});
            skLineSegment(sketch, "E27.6.3.1", {"start": v(-73.03, -28.38) * mm, "end": v(-57.15, -21.62) * mm});
            skLineSegment(sketch, "E27.6.3.2", {"start": v(-57.15, -21.62) * mm, "end": v(-41.28, -28.38) * mm});
            skLineSegment(sketch, "E27.6.3.3", {"start": v(-41.28, -28.38) * mm, "end": v(-57.15, -35.15) * mm});
            skLineSegment(sketch, "E27.6.4.0", {"start": v(-57.15, -16.22) * mm, "end": v(-73.03, -9.46) * mm});
            skLineSegment(sketch, "E27.6.4.1", {"start": v(-73.03, -9.46) * mm, "end": v(-57.15, -2.7) * mm});
            skLineSegment(sketch, "E27.6.4.2", {"start": v(-57.15, -2.7) * mm, "end": v(-41.28, -9.46) * mm});
            skLineSegment(sketch, "E27.6.4.3", {"start": v(-41.28, -9.46) * mm, "end": v(-57.15, -16.22) * mm});
            skLineSegment(sketch, "E27.6.5.0", {"start": v(-57.15, 2.7) * mm, "end": v(-73.03, 9.46) * mm});
            skLineSegment(sketch, "E27.6.5.1", {"start": v(-73.03, 9.46) * mm, "end": v(-57.15, 16.22) * mm});
            skLineSegment(sketch, "E27.6.5.2", {"start": v(-57.15, 16.22) * mm, "end": v(-41.28, 9.46) * mm});
            skLineSegment(sketch, "E27.6.5.3", {"start": v(-41.28, 9.46) * mm, "end": v(-57.15, 2.7) * mm});
            skLineSegment(sketch, "E27.6.6.0", {"start": v(-57.15, 21.62) * mm, "end": v(-73.03, 28.38) * mm});
            skLineSegment(sketch, "E27.6.6.1", {"start": v(-73.03, 28.38) * mm, "end": v(-57.15, 35.15) * mm});
            skLineSegment(sketch, "E27.6.6.2", {"start": v(-57.15, 35.15) * mm, "end": v(-41.28, 28.38) * mm});
            skLineSegment(sketch, "E27.6.6.3", {"start": v(-41.28, 28.38) * mm, "end": v(-57.15, 21.62) * mm});
            skLineSegment(sketch, "E27.6.7.0", {"start": v(-57.15, 40.54) * mm, "end": v(-73.03, 47.3) * mm});
            skLineSegment(sketch, "E27.6.7.1", {"start": v(-73.03, 47.3) * mm, "end": v(-57.15, 54.07) * mm});
            skLineSegment(sketch, "E27.6.7.2", {"start": v(-57.15, 54.07) * mm, "end": v(-41.28, 47.3) * mm});
            skLineSegment(sketch, "E27.6.7.3", {"start": v(-41.28, 47.3) * mm, "end": v(-57.15, 40.54) * mm});
            skLineSegment(sketch, "E27.6.8.0", {"start": v(-57.15, 59.47) * mm, "end": v(-73.03, 66.23) * mm});
            skLineSegment(sketch, "E27.6.8.1", {"start": v(-73.03, 66.23) * mm, "end": v(-57.15, 73) * mm});
            skLineSegment(sketch, "E27.6.8.2", {"start": v(-57.15, 73) * mm, "end": v(-41.28, 66.23) * mm});
            skLineSegment(sketch, "E27.6.8.3", {"start": v(-41.28, 66.23) * mm, "end": v(-57.15, 59.47) * mm});
            skLineSegment(sketch, "E27.6.9.0", {"start": v(-57.15, 78.4) * mm, "end": v(-73.03, 85.15) * mm});
            skLineSegment(sketch, "E27.6.9.1", {"start": v(-73.03, 85.15) * mm, "end": v(-57.15, 91.92) * mm});
            skLineSegment(sketch, "E27.6.9.2", {"start": v(-57.15, 91.92) * mm, "end": v(-41.28, 85.15) * mm});
            skLineSegment(sketch, "E27.6.9.3", {"start": v(-41.28, 85.15) * mm, "end": v(-57.15, 78.4) * mm});
            skLineSegment(sketch, "E27.7.0.0", {"start": v(-95.25, -91.92) * mm, "end": v(-111.13, -85.15) * mm});
            skLineSegment(sketch, "E27.7.0.1", {"start": v(-111.13, -85.15) * mm, "end": v(-95.25, -78.4) * mm});
            skLineSegment(sketch, "E27.7.0.2", {"start": v(-95.25, -78.4) * mm, "end": v(-79.38, -85.15) * mm});
            skLineSegment(sketch, "E27.7.0.3", {"start": v(-79.38, -85.15) * mm, "end": v(-95.25, -91.92) * mm});
            skLineSegment(sketch, "E27.7.1.0", {"start": v(-95.25, -73) * mm, "end": v(-111.13, -66.23) * mm});
            skLineSegment(sketch, "E27.7.1.1", {"start": v(-111.13, -66.23) * mm, "end": v(-95.25, -59.47) * mm});
            skLineSegment(sketch, "E27.7.1.2", {"start": v(-95.25, -59.47) * mm, "end": v(-79.38, -66.23) * mm});
            skLineSegment(sketch, "E27.7.1.3", {"start": v(-79.38, -66.23) * mm, "end": v(-95.25, -73) * mm});
            skLineSegment(sketch, "E27.7.2.0", {"start": v(-95.25, -54.07) * mm, "end": v(-111.13, -47.3) * mm});
            skLineSegment(sketch, "E27.7.2.1", {"start": v(-111.13, -47.3) * mm, "end": v(-95.25, -40.54) * mm});
            skLineSegment(sketch, "E27.7.2.2", {"start": v(-95.25, -40.54) * mm, "end": v(-79.38, -47.3) * mm});
            skLineSegment(sketch, "E27.7.2.3", {"start": v(-79.38, -47.3) * mm, "end": v(-95.25, -54.07) * mm});
            skLineSegment(sketch, "E27.7.3.0", {"start": v(-95.25, -35.15) * mm, "end": v(-111.13, -28.38) * mm});
            skLineSegment(sketch, "E27.7.3.1", {"start": v(-111.13, -28.38) * mm, "end": v(-95.25, -21.62) * mm});
            skLineSegment(sketch, "E27.7.3.2", {"start": v(-95.25, -21.62) * mm, "end": v(-79.38, -28.38) * mm});
            skLineSegment(sketch, "E27.7.3.3", {"start": v(-79.38, -28.38) * mm, "end": v(-95.25, -35.15) * mm});
            skLineSegment(sketch, "E27.7.4.0", {"start": v(-95.25, -16.22) * mm, "end": v(-111.13, -9.46) * mm});
            skLineSegment(sketch, "E27.7.4.1", {"start": v(-111.13, -9.46) * mm, "end": v(-95.25, -2.7) * mm});
            skLineSegment(sketch, "E27.7.4.2", {"start": v(-95.25, -2.7) * mm, "end": v(-79.38, -9.46) * mm});
            skLineSegment(sketch, "E27.7.4.3", {"start": v(-79.38, -9.46) * mm, "end": v(-95.25, -16.22) * mm});
            skLineSegment(sketch, "E27.7.5.0", {"start": v(-95.25, 2.7) * mm, "end": v(-111.13, 9.46) * mm});
            skLineSegment(sketch, "E27.7.5.1", {"start": v(-111.13, 9.46) * mm, "end": v(-95.25, 16.22) * mm});
            skLineSegment(sketch, "E27.7.5.2", {"start": v(-95.25, 16.22) * mm, "end": v(-79.38, 9.46) * mm});
            skLineSegment(sketch, "E27.7.5.3", {"start": v(-79.38, 9.46) * mm, "end": v(-95.25, 2.7) * mm});
            skLineSegment(sketch, "E27.7.6.0", {"start": v(-95.25, 21.62) * mm, "end": v(-111.13, 28.38) * mm});
            skLineSegment(sketch, "E27.7.6.1", {"start": v(-111.13, 28.38) * mm, "end": v(-95.25, 35.15) * mm});
            skLineSegment(sketch, "E27.7.6.2", {"start": v(-95.25, 35.15) * mm, "end": v(-79.38, 28.38) * mm});
            skLineSegment(sketch, "E27.7.6.3", {"start": v(-79.38, 28.38) * mm, "end": v(-95.25, 21.62) * mm});
            skLineSegment(sketch, "E27.7.7.0", {"start": v(-95.25, 40.54) * mm, "end": v(-111.13, 47.3) * mm});
            skLineSegment(sketch, "E27.7.7.1", {"start": v(-111.13, 47.3) * mm, "end": v(-95.25, 54.07) * mm});
            skLineSegment(sketch, "E27.7.7.2", {"start": v(-95.25, 54.07) * mm, "end": v(-79.38, 47.3) * mm});
            skLineSegment(sketch, "E27.7.7.3", {"start": v(-79.38, 47.3) * mm, "end": v(-95.25, 40.54) * mm});
            skLineSegment(sketch, "E27.7.8.0", {"start": v(-95.25, 59.47) * mm, "end": v(-111.13, 66.23) * mm});
            skLineSegment(sketch, "E27.7.8.1", {"start": v(-111.13, 66.23) * mm, "end": v(-95.25, 73) * mm});
            skLineSegment(sketch, "E27.7.8.2", {"start": v(-95.25, 73) * mm, "end": v(-79.38, 66.23) * mm});
            skLineSegment(sketch, "E27.7.8.3", {"start": v(-79.38, 66.23) * mm, "end": v(-95.25, 59.47) * mm});
            skLineSegment(sketch, "E27.7.9.0", {"start": v(-95.25, 78.4) * mm, "end": v(-111.13, 85.15) * mm});
            skLineSegment(sketch, "E27.7.9.1", {"start": v(-111.13, 85.15) * mm, "end": v(-95.25, 91.92) * mm});
            skLineSegment(sketch, "E27.7.9.2", {"start": v(-95.25, 91.92) * mm, "end": v(-79.38, 85.15) * mm});
            skLineSegment(sketch, "E27.7.9.3", {"start": v(-79.38, 85.15) * mm, "end": v(-95.25, 78.4) * mm});
            skLineSegment(sketch, "E27.8.0.0", {"start": v(-133.35, -91.92) * mm, "end": v(-149.23, -85.15) * mm});
            skLineSegment(sketch, "E27.8.0.1", {"start": v(-149.23, -85.15) * mm, "end": v(-133.35, -78.4) * mm});
            skLineSegment(sketch, "E27.8.0.2", {"start": v(-133.35, -78.4) * mm, "end": v(-117.48, -85.15) * mm});
            skLineSegment(sketch, "E27.8.0.3", {"start": v(-117.48, -85.15) * mm, "end": v(-133.35, -91.92) * mm});
            skLineSegment(sketch, "E27.8.1.0", {"start": v(-133.35, -73) * mm, "end": v(-149.23, -66.23) * mm});
            skLineSegment(sketch, "E27.8.1.1", {"start": v(-149.23, -66.23) * mm, "end": v(-133.35, -59.47) * mm});
            skLineSegment(sketch, "E27.8.1.2", {"start": v(-133.35, -59.47) * mm, "end": v(-117.48, -66.23) * mm});
            skLineSegment(sketch, "E27.8.1.3", {"start": v(-117.48, -66.23) * mm, "end": v(-133.35, -73) * mm});
            skLineSegment(sketch, "E27.8.2.0", {"start": v(-133.35, -54.07) * mm, "end": v(-149.23, -47.3) * mm});
            skLineSegment(sketch, "E27.8.2.1", {"start": v(-149.23, -47.3) * mm, "end": v(-133.35, -40.54) * mm});
            skLineSegment(sketch, "E27.8.2.2", {"start": v(-133.35, -40.54) * mm, "end": v(-117.48, -47.3) * mm});
            skLineSegment(sketch, "E27.8.2.3", {"start": v(-117.48, -47.3) * mm, "end": v(-133.35, -54.07) * mm});
            skLineSegment(sketch, "E27.8.3.0", {"start": v(-133.35, -35.15) * mm, "end": v(-149.23, -28.38) * mm});
            skLineSegment(sketch, "E27.8.3.1", {"start": v(-149.23, -28.38) * mm, "end": v(-133.35, -21.62) * mm});
            skLineSegment(sketch, "E27.8.3.2", {"start": v(-133.35, -21.62) * mm, "end": v(-117.48, -28.38) * mm});
            skLineSegment(sketch, "E27.8.3.3", {"start": v(-117.48, -28.38) * mm, "end": v(-133.35, -35.15) * mm});
            skLineSegment(sketch, "E27.8.4.0", {"start": v(-133.35, -16.22) * mm, "end": v(-149.23, -9.46) * mm});
            skLineSegment(sketch, "E27.8.4.1", {"start": v(-149.23, -9.46) * mm, "end": v(-133.35, -2.7) * mm});
            skLineSegment(sketch, "E27.8.4.2", {"start": v(-133.35, -2.7) * mm, "end": v(-117.48, -9.46) * mm});
            skLineSegment(sketch, "E27.8.4.3", {"start": v(-117.48, -9.46) * mm, "end": v(-133.35, -16.22) * mm});
            skLineSegment(sketch, "E27.8.5.0", {"start": v(-133.35, 2.7) * mm, "end": v(-149.23, 9.46) * mm});
            skLineSegment(sketch, "E27.8.5.1", {"start": v(-149.23, 9.46) * mm, "end": v(-133.35, 16.22) * mm});
            skLineSegment(sketch, "E27.8.5.2", {"start": v(-133.35, 16.22) * mm, "end": v(-117.48, 9.46) * mm});
            skLineSegment(sketch, "E27.8.5.3", {"start": v(-117.48, 9.46) * mm, "end": v(-133.35, 2.7) * mm});
            skLineSegment(sketch, "E27.8.6.0", {"start": v(-133.35, 21.62) * mm, "end": v(-149.23, 28.38) * mm});
            skLineSegment(sketch, "E27.8.6.1", {"start": v(-149.23, 28.38) * mm, "end": v(-133.35, 35.15) * mm});
            skLineSegment(sketch, "E27.8.6.2", {"start": v(-133.35, 35.15) * mm, "end": v(-117.48, 28.38) * mm});
            skLineSegment(sketch, "E27.8.6.3", {"start": v(-117.48, 28.38) * mm, "end": v(-133.35, 21.62) * mm});
            skLineSegment(sketch, "E27.8.7.0", {"start": v(-133.35, 40.54) * mm, "end": v(-149.23, 47.3) * mm});
            skLineSegment(sketch, "E27.8.7.1", {"start": v(-149.23, 47.3) * mm, "end": v(-133.35, 54.07) * mm});
            skLineSegment(sketch, "E27.8.7.2", {"start": v(-133.35, 54.07) * mm, "end": v(-117.48, 47.3) * mm});
            skLineSegment(sketch, "E27.8.7.3", {"start": v(-117.48, 47.3) * mm, "end": v(-133.35, 40.54) * mm});
            skLineSegment(sketch, "E27.8.8.0", {"start": v(-133.35, 59.47) * mm, "end": v(-149.23, 66.23) * mm});
            skLineSegment(sketch, "E27.8.8.1", {"start": v(-149.23, 66.23) * mm, "end": v(-133.35, 73) * mm});
            skLineSegment(sketch, "E27.8.8.2", {"start": v(-133.35, 73) * mm, "end": v(-117.48, 66.23) * mm});
            skLineSegment(sketch, "E27.8.8.3", {"start": v(-117.48, 66.23) * mm, "end": v(-133.35, 59.47) * mm});
            skLineSegment(sketch, "E27.8.9.0", {"start": v(-133.35, 78.4) * mm, "end": v(-149.23, 85.15) * mm});
            skLineSegment(sketch, "E27.8.9.1", {"start": v(-149.23, 85.15) * mm, "end": v(-133.35, 91.92) * mm});
            skLineSegment(sketch, "E27.8.9.2", {"start": v(-133.35, 91.92) * mm, "end": v(-117.48, 85.15) * mm});
            skLineSegment(sketch, "E27.8.9.3", {"start": v(-117.48, 85.15) * mm, "end": v(-133.35, 78.4) * mm});
            skLineSegment(sketch, "E27.9.0.0", {"start": v(-171.45, -91.92) * mm, "end": v(-187.33, -85.15) * mm});
            skLineSegment(sketch, "E27.9.0.1", {"start": v(-187.33, -85.15) * mm, "end": v(-171.45, -78.4) * mm});
            skLineSegment(sketch, "E27.9.0.2", {"start": v(-171.45, -78.4) * mm, "end": v(-155.58, -85.15) * mm});
            skLineSegment(sketch, "E27.9.0.3", {"start": v(-155.58, -85.15) * mm, "end": v(-171.45, -91.92) * mm});
            skLineSegment(sketch, "E27.9.1.0", {"start": v(-171.45, -73) * mm, "end": v(-187.33, -66.23) * mm});
            skLineSegment(sketch, "E27.9.1.1", {"start": v(-187.33, -66.23) * mm, "end": v(-171.45, -59.47) * mm});
            skLineSegment(sketch, "E27.9.1.2", {"start": v(-171.45, -59.47) * mm, "end": v(-155.58, -66.23) * mm});
            skLineSegment(sketch, "E27.9.1.3", {"start": v(-155.58, -66.23) * mm, "end": v(-171.45, -73) * mm});
            skLineSegment(sketch, "E27.9.2.0", {"start": v(-171.45, -54.07) * mm, "end": v(-187.33, -47.3) * mm});
            skLineSegment(sketch, "E27.9.2.1", {"start": v(-187.33, -47.3) * mm, "end": v(-171.45, -40.54) * mm});
            skLineSegment(sketch, "E27.9.2.2", {"start": v(-171.45, -40.54) * mm, "end": v(-155.58, -47.3) * mm});
            skLineSegment(sketch, "E27.9.2.3", {"start": v(-155.58, -47.3) * mm, "end": v(-171.45, -54.07) * mm});
            skLineSegment(sketch, "E27.9.3.0", {"start": v(-171.45, -35.15) * mm, "end": v(-187.33, -28.38) * mm});
            skLineSegment(sketch, "E27.9.3.1", {"start": v(-187.33, -28.38) * mm, "end": v(-171.45, -21.62) * mm});
            skLineSegment(sketch, "E27.9.3.2", {"start": v(-171.45, -21.62) * mm, "end": v(-155.58, -28.38) * mm});
            skLineSegment(sketch, "E27.9.3.3", {"start": v(-155.58, -28.38) * mm, "end": v(-171.45, -35.15) * mm});
            skLineSegment(sketch, "E27.9.4.0", {"start": v(-171.45, -16.22) * mm, "end": v(-187.33, -9.46) * mm});
            skLineSegment(sketch, "E27.9.4.1", {"start": v(-187.33, -9.46) * mm, "end": v(-171.45, -2.7) * mm});
            skLineSegment(sketch, "E27.9.4.2", {"start": v(-171.45, -2.7) * mm, "end": v(-155.58, -9.46) * mm});
            skLineSegment(sketch, "E27.9.4.3", {"start": v(-155.58, -9.46) * mm, "end": v(-171.45, -16.22) * mm});
            skLineSegment(sketch, "E27.9.5.0", {"start": v(-171.45, 2.7) * mm, "end": v(-187.33, 9.46) * mm});
            skLineSegment(sketch, "E27.9.5.1", {"start": v(-187.33, 9.46) * mm, "end": v(-171.45, 16.22) * mm});
            skLineSegment(sketch, "E27.9.5.2", {"start": v(-171.45, 16.22) * mm, "end": v(-155.58, 9.46) * mm});
            skLineSegment(sketch, "E27.9.5.3", {"start": v(-155.58, 9.46) * mm, "end": v(-171.45, 2.7) * mm});
            skLineSegment(sketch, "E27.9.6.0", {"start": v(-171.45, 21.62) * mm, "end": v(-187.33, 28.38) * mm});
            skLineSegment(sketch, "E27.9.6.1", {"start": v(-187.33, 28.38) * mm, "end": v(-171.45, 35.15) * mm});
            skLineSegment(sketch, "E27.9.6.2", {"start": v(-171.45, 35.15) * mm, "end": v(-155.58, 28.38) * mm});
            skLineSegment(sketch, "E27.9.6.3", {"start": v(-155.58, 28.38) * mm, "end": v(-171.45, 21.62) * mm});
            skLineSegment(sketch, "E27.9.7.0", {"start": v(-171.45, 40.54) * mm, "end": v(-187.33, 47.3) * mm});
            skLineSegment(sketch, "E27.9.7.1", {"start": v(-187.33, 47.3) * mm, "end": v(-171.45, 54.07) * mm});
            skLineSegment(sketch, "E27.9.7.2", {"start": v(-171.45, 54.07) * mm, "end": v(-155.58, 47.3) * mm});
            skLineSegment(sketch, "E27.9.7.3", {"start": v(-155.58, 47.3) * mm, "end": v(-171.45, 40.54) * mm});
            skLineSegment(sketch, "E27.9.8.0", {"start": v(-171.45, 59.47) * mm, "end": v(-187.33, 66.23) * mm});
            skLineSegment(sketch, "E27.9.8.1", {"start": v(-187.33, 66.23) * mm, "end": v(-171.45, 73) * mm});
            skLineSegment(sketch, "E27.9.8.2", {"start": v(-171.45, 73) * mm, "end": v(-155.58, 66.23) * mm});
            skLineSegment(sketch, "E27.9.8.3", {"start": v(-155.58, 66.23) * mm, "end": v(-171.45, 59.47) * mm});
            skLineSegment(sketch, "E27.9.9.0", {"start": v(-171.45, 78.4) * mm, "end": v(-187.33, 85.15) * mm});
            skLineSegment(sketch, "E27.9.9.1", {"start": v(-187.33, 85.15) * mm, "end": v(-171.45, 91.92) * mm});
            skLineSegment(sketch, "E27.9.9.2", {"start": v(-171.45, 91.92) * mm, "end": v(-155.58, 85.15) * mm});
            skLineSegment(sketch, "E27.9.9.3", {"start": v(-155.58, 85.15) * mm, "end": v(-171.45, 78.4) * mm});
            skLineSegment(sketch, "E27.direction1", {"start": v(155.57, -85.15) * mm, "end": v(117.47, -85.15) * mm, "construction": true});
            skLineSegment(sketch, "E27.direction2", {"start": v(155.57, -85.15) * mm, "end": v(155.57, -66.23) * mm, "construction": true});
            skSolve(sketch);
        }
        {
            var Q0;
            Q0=qSketchRegion(id+"F6",true);
            extrude(context, id + "F7", {"entities" : qUnion([Q0]), "operationType" : NewBodyOperationType.REMOVE, "oppositeDirection" : true, "depth" : 25.4 * mm});
        }
    });
